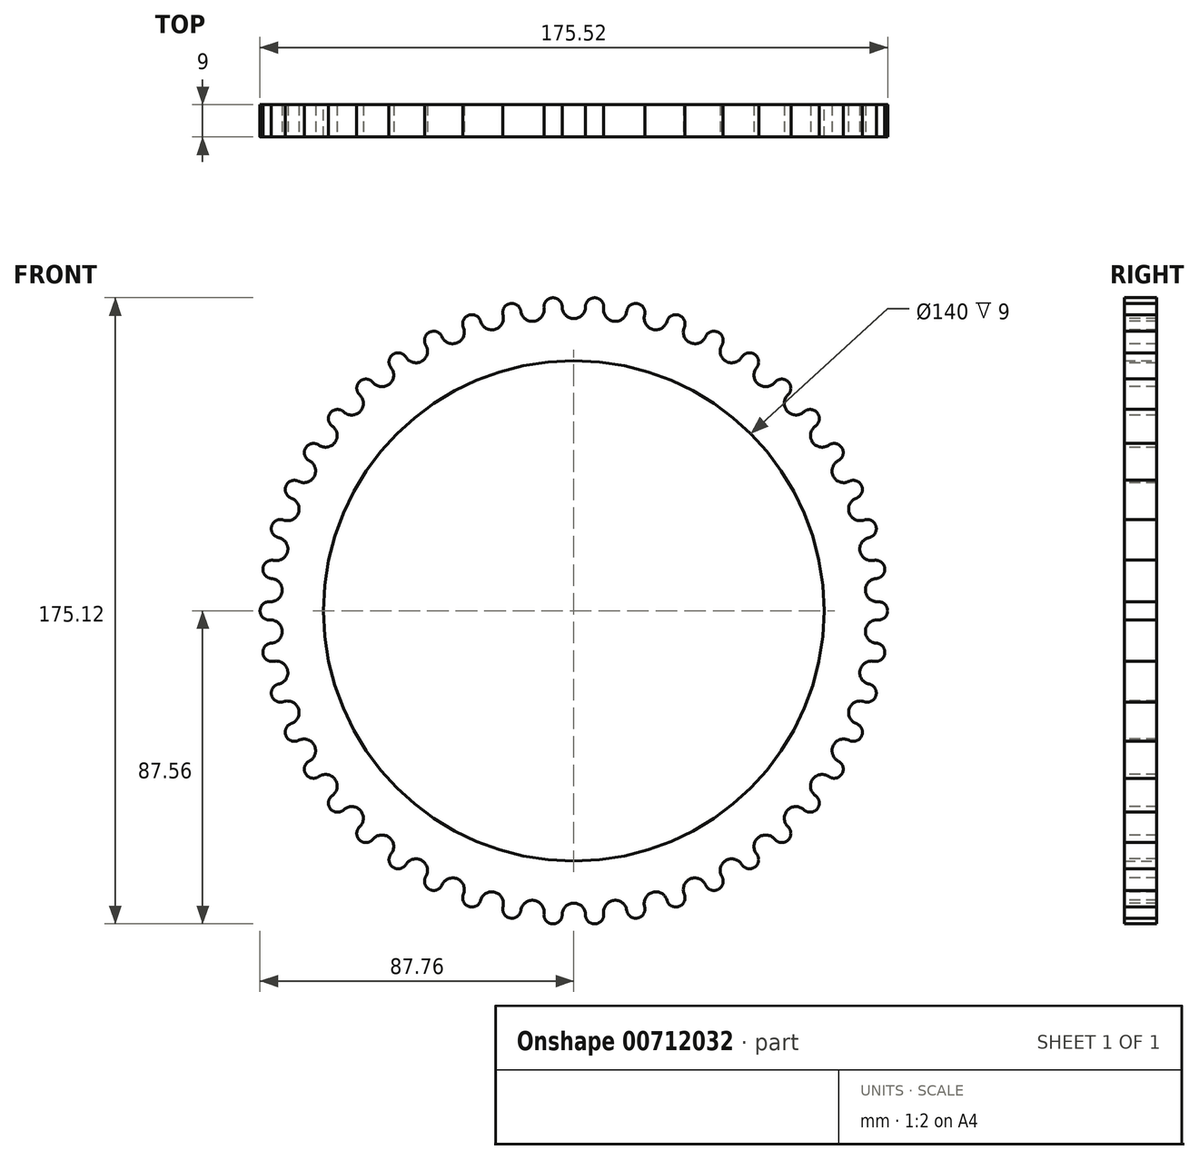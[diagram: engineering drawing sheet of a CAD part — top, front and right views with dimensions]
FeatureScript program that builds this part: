
annotation { "Feature Type Name" : "Feature", "Feature Type Description" : "" }
export const myFeature = defineFeature(function(context is Context, id is Id, definition is map)
    precondition{}
    {
        {
            var Q0;
            Q0=qCreatedBy(makeId("Front.planeOp"),FACE);
            var sketch = newSketch(context, id + "F0", { "sketchPlane" : qUnion([Q0])});
            skCircle(sketch, "E0", {"center": v(0, 0) * mm, "radius": 70 * mm});
            skCircle(sketch, "E1", {"center": v(0, 0) * mm, "radius": 80 * mm});
            skArc(sketch, "E2", {"start": v(4.8, -89.87) * mm, "mid": v(0, 90) * mm, "end": v(-4.8, -89.87) * mm});
            skArc(sketch, "E3", {"start": v(3, -85) * mm, "mid": v(0, -82) * mm, "end": v(-3, -85) * mm});
            skPoint(sketch, "E4.orphan", {"position": v(0, -90) * mm});
            skPoint(sketch, "E5.visualSharp", {"position": v(-3, -89.95) * mm});
            skPoint(sketch, "E6.visualSharp", {"position": v(3, -89.95) * mm});
            skLineSegment(sketch, "E7", {"start": v(0, -90) * mm, "end": v(0, -85) * mm});
            skLineSegment(sketch, "E8.1.0", {"start": v(3, 85) * mm, "end": v(3, 88.91) * mm});
            skArc(sketch, "E8.1.1", {"start": v(4.04, 89.9) * mm, "mid": v(3.3, 89.63) * mm, "end": v(3, 88.91) * mm});
            skArc(sketch, "E8.1.2", {"start": v(-3, 85) * mm, "mid": v(0, 82) * mm, "end": v(3, 85) * mm});
            skLineSegment(sketch, "E8.1.3", {"start": v(-3, 85) * mm, "end": v(-3, 88.91) * mm});
            skArc(sketch, "E8.1.4", {"start": v(-3, 88.91) * mm, "mid": v(-3.3, 89.63) * mm, "end": v(-4.04, 89.9) * mm});
            skLineSegment(sketch, "E9", {"start": v(-3, -86.96) * mm, "end": v(-3.8, -89.2) * mm});
            skLineSegment(sketch, "E10", {"start": v(3, -86.96) * mm, "end": v(3.8, -89.2) * mm});
            skPoint(sketch, "E11.visualSharp", {"position": v(-4.04, -89.9) * mm});
            skArc(sketch, "E11.filletArc", {"start": v(-4.8, -89.87) * mm, "mid": v(-4.18, -89.7) * mm, "end": v(-3.8, -89.2) * mm});
            skPoint(sketch, "E12.visualSharp", {"position": v(4.04, -89.9) * mm});
            skArc(sketch, "E12.filletArc", {"start": v(3.8, -89.2) * mm, "mid": v(4.18, -89.7) * mm, "end": v(4.8, -89.87) * mm});
            skArc(sketch, "E13.1.0", {"start": v(7.49, -89.69) * mm, "mid": v(8.07, -89.44) * mm, "end": v(8.39, -88.9) * mm});
            skLineSegment(sketch, "E13.1.1", {"start": v(8.87, -86.55) * mm, "end": v(8.39, -88.9) * mm});
            skLineSegment(sketch, "E13.1.2", {"start": v(8.6, -84.62) * mm, "end": v(9.13, -88.5) * mm});
            skArc(sketch, "E13.1.3", {"start": v(14.55, -83.8) * mm, "mid": v(11.17, -81.24) * mm, "end": v(8.6, -84.62) * mm});
            skLineSegment(sketch, "E13.1.4", {"start": v(14.55, -83.8) * mm, "end": v(15.08, -87.67) * mm});
            skLineSegment(sketch, "E13.1.5", {"start": v(14.81, -85.74) * mm, "end": v(15.9, -87.86) * mm});
            skArc(sketch, "E13.1.6", {"start": v(15.9, -87.86) * mm, "mid": v(16.36, -88.3) * mm, "end": v(16.99, -88.38) * mm});
            skArc(sketch, "E13.2.0", {"start": v(19.63, -87.83) * mm, "mid": v(20.17, -87.5) * mm, "end": v(20.41, -86.92) * mm});
            skLineSegment(sketch, "E13.2.1", {"start": v(20.57, -84.54) * mm, "end": v(20.41, -86.92) * mm});
            skLineSegment(sketch, "E13.2.2", {"start": v(20.04, -82.66) * mm, "end": v(21.1, -86.42) * mm});
            skArc(sketch, "E13.2.3", {"start": v(25.82, -81.04) * mm, "mid": v(22.12, -78.96) * mm, "end": v(20.04, -82.66) * mm});
            skLineSegment(sketch, "E13.2.4", {"start": v(25.82, -81.04) * mm, "end": v(26.88, -84.8) * mm});
            skLineSegment(sketch, "E13.2.5", {"start": v(26.35, -82.92) * mm, "end": v(27.72, -84.87) * mm});
            skArc(sketch, "E13.2.6", {"start": v(27.72, -84.87) * mm, "mid": v(28.23, -85.25) * mm, "end": v(28.86, -85.25) * mm});
            skArc(sketch, "E13.3.0", {"start": v(31.4, -84.34) * mm, "mid": v(31.9, -83.95) * mm, "end": v(32.06, -83.33) * mm});
            skLineSegment(sketch, "E13.3.1", {"start": v(31.9, -80.95) * mm, "end": v(32.06, -83.33) * mm});
            skLineSegment(sketch, "E13.3.2", {"start": v(31.11, -79.16) * mm, "end": v(32.67, -82.74) * mm});
            skArc(sketch, "E13.3.3", {"start": v(36.62, -76.77) * mm, "mid": v(32.67, -75.21) * mm, "end": v(31.11, -79.16) * mm});
            skLineSegment(sketch, "E13.3.4", {"start": v(36.62, -76.77) * mm, "end": v(38.17, -80.35) * mm});
            skLineSegment(sketch, "E13.3.5", {"start": v(37.4, -78.56) * mm, "end": v(39.02, -80.3) * mm});
            skArc(sketch, "E13.3.6", {"start": v(39.02, -80.3) * mm, "mid": v(39.58, -80.61) * mm, "end": v(40.2, -80.52) * mm});
            skArc(sketch, "E13.4.0", {"start": v(42.6, -79.28) * mm, "mid": v(43.03, -78.82) * mm, "end": v(43.1, -78.2) * mm});
            skLineSegment(sketch, "E13.4.1", {"start": v(42.62, -75.85) * mm, "end": v(43.1, -78.2) * mm});
            skLineSegment(sketch, "E13.4.2", {"start": v(41.6, -74.18) * mm, "end": v(43.63, -77.53) * mm});
            skArc(sketch, "E13.4.3", {"start": v(46.73, -71.07) * mm, "mid": v(42.6, -70.06) * mm, "end": v(41.6, -74.18) * mm});
            skLineSegment(sketch, "E13.4.4", {"start": v(46.73, -71.07) * mm, "end": v(48.76, -74.4) * mm});
            skLineSegment(sketch, "E13.4.5", {"start": v(47.74, -72.74) * mm, "end": v(49.6, -74.25) * mm});
            skArc(sketch, "E13.4.6", {"start": v(49.6, -74.25) * mm, "mid": v(50.18, -74.47) * mm, "end": v(50.8, -74.3) * mm});
            skArc(sketch, "E13.5.0", {"start": v(53, -72.74) * mm, "mid": v(53.37, -72.23) * mm, "end": v(53.35, -71.6) * mm});
            skLineSegment(sketch, "E13.5.1", {"start": v(52.55, -69.35) * mm, "end": v(53.35, -71.6) * mm});
            skLineSegment(sketch, "E13.5.2", {"start": v(51.32, -67.83) * mm, "end": v(53.78, -70.86) * mm});
            skArc(sketch, "E13.5.3", {"start": v(55.97, -64.04) * mm, "mid": v(51.75, -63.6) * mm, "end": v(51.32, -67.83) * mm});
            skLineSegment(sketch, "E13.5.4", {"start": v(55.97, -64.04) * mm, "end": v(58.44, -67.08) * mm});
            skLineSegment(sketch, "E13.5.5", {"start": v(57.2, -65.56) * mm, "end": v(59.24, -66.8) * mm});
            skArc(sketch, "E13.5.6", {"start": v(59.24, -66.8) * mm, "mid": v(59.86, -66.94) * mm, "end": v(60.44, -66.7) * mm});
            skArc(sketch, "E13.6.0", {"start": v(62.41, -64.85) * mm, "mid": v(62.7, -64.29) * mm, "end": v(62.6, -63.66) * mm});
            skLineSegment(sketch, "E13.6.1", {"start": v(61.5, -61.54) * mm, "end": v(62.6, -63.66) * mm});
            skLineSegment(sketch, "E13.6.2", {"start": v(60.07, -60.2) * mm, "end": v(62.93, -62.88) * mm});
            skArc(sketch, "E13.6.3", {"start": v(64.17, -55.82) * mm, "mid": v(59.93, -55.97) * mm, "end": v(60.07, -60.2) * mm});
            skLineSegment(sketch, "E13.6.4", {"start": v(64.17, -55.82) * mm, "end": v(67.03, -58.5) * mm});
            skLineSegment(sketch, "E13.6.5", {"start": v(65.6, -57.16) * mm, "end": v(67.79, -58.11) * mm});
            skArc(sketch, "E13.6.6", {"start": v(67.79, -58.11) * mm, "mid": v(68.42, -58.17) * mm, "end": v(68.95, -57.84) * mm});
            skArc(sketch, "E13.7.0", {"start": v(70.66, -55.74) * mm, "mid": v(70.87, -55.15) * mm, "end": v(70.7, -54.55) * mm});
            skLineSegment(sketch, "E13.7.1", {"start": v(69.3, -52.6) * mm, "end": v(70.7, -54.55) * mm});
            skLineSegment(sketch, "E13.7.2", {"start": v(67.71, -51.47) * mm, "end": v(70.9, -53.72) * mm});
            skArc(sketch, "E13.7.3", {"start": v(71.17, -46.57) * mm, "mid": v(67, -47.29) * mm, "end": v(67.71, -51.47) * mm});
            skLineSegment(sketch, "E13.7.4", {"start": v(71.17, -46.57) * mm, "end": v(74.37, -48.82) * mm});
            skLineSegment(sketch, "E13.7.5", {"start": v(72.77, -47.7) * mm, "end": v(75.07, -48.34) * mm});
            skArc(sketch, "E13.7.6", {"start": v(75.07, -48.34) * mm, "mid": v(75.7, -48.31) * mm, "end": v(76.19, -47.91) * mm});
            skArc(sketch, "E13.8.0", {"start": v(77.6, -45.6) * mm, "mid": v(77.72, -44.99) * mm, "end": v(77.46, -44.41) * mm});
            skLineSegment(sketch, "E13.8.1", {"start": v(75.83, -42.67) * mm, "end": v(77.46, -44.41) * mm});
            skLineSegment(sketch, "E13.8.2", {"start": v(74.1, -41.77) * mm, "end": v(77.56, -43.57) * mm});
            skArc(sketch, "E13.8.3", {"start": v(76.85, -36.44) * mm, "mid": v(72.8, -37.73) * mm, "end": v(74.1, -41.77) * mm});
            skLineSegment(sketch, "E13.8.4", {"start": v(76.85, -36.44) * mm, "end": v(80.32, -38.24) * mm});
            skLineSegment(sketch, "E13.8.5", {"start": v(78.59, -37.34) * mm, "end": v(80.95, -37.67) * mm});
            skArc(sketch, "E13.8.6", {"start": v(80.95, -37.67) * mm, "mid": v(81.57, -37.56) * mm, "end": v(82, -37.1) * mm});
            skArc(sketch, "E13.9.0", {"start": v(83.08, -34.61) * mm, "mid": v(83.12, -33.98) * mm, "end": v(82.79, -33.45) * mm});
            skLineSegment(sketch, "E13.9.1", {"start": v(80.93, -31.95) * mm, "end": v(82.79, -33.45) * mm});
            skLineSegment(sketch, "E13.9.2", {"start": v(79.09, -31.3) * mm, "end": v(82.77, -32.6) * mm});
            skArc(sketch, "E13.9.3", {"start": v(81.1, -25.64) * mm, "mid": v(77.27, -27.46) * mm, "end": v(79.09, -31.3) * mm});
            skLineSegment(sketch, "E13.9.4", {"start": v(81.1, -25.64) * mm, "end": v(84.78, -26.95) * mm});
            skLineSegment(sketch, "E13.9.5", {"start": v(82.94, -26.3) * mm, "end": v(85.33, -26.3) * mm});
            skArc(sketch, "E13.9.6", {"start": v(85.33, -26.3) * mm, "mid": v(85.93, -26.1) * mm, "end": v(86.29, -25.58) * mm});
            skArc(sketch, "E13.10.0", {"start": v(87.02, -22.98) * mm, "mid": v(86.98, -22.35) * mm, "end": v(86.57, -21.87) * mm});
            skLineSegment(sketch, "E13.10.1", {"start": v(84.53, -20.63) * mm, "end": v(86.57, -21.87) * mm});
            skLineSegment(sketch, "E13.10.2", {"start": v(82.61, -20.23) * mm, "end": v(86.44, -21.03) * mm});
            skArc(sketch, "E13.10.3", {"start": v(83.83, -14.36) * mm, "mid": v(80.28, -16.68) * mm, "end": v(82.61, -20.23) * mm});
            skLineSegment(sketch, "E13.10.4", {"start": v(83.83, -14.36) * mm, "end": v(87.66, -15.15) * mm});
            skLineSegment(sketch, "E13.10.5", {"start": v(85.75, -14.75) * mm, "end": v(88.11, -14.43) * mm});
            skArc(sketch, "E13.10.6", {"start": v(88.11, -14.43) * mm, "mid": v(88.68, -14.15) * mm, "end": v(88.97, -13.6) * mm});
            skArc(sketch, "E13.11.0", {"start": v(89.34, -10.91) * mm, "mid": v(89.21, -10.3) * mm, "end": v(88.74, -9.88) * mm});
            skLineSegment(sketch, "E13.11.1", {"start": v(86.55, -8.93) * mm, "end": v(88.74, -9.88) * mm});
            skLineSegment(sketch, "E13.11.2", {"start": v(84.6, -8.8) * mm, "end": v(88.5, -9.06) * mm});
            skArc(sketch, "E13.11.3", {"start": v(85, -2.8) * mm, "mid": v(81.8, -5.6) * mm, "end": v(84.6, -8.8) * mm});
            skLineSegment(sketch, "E13.11.4", {"start": v(85, -2.8) * mm, "end": v(88.9, -3.07) * mm});
            skLineSegment(sketch, "E13.11.5", {"start": v(86.96, -2.94) * mm, "end": v(89.26, -2.3) * mm});
            skArc(sketch, "E13.11.6", {"start": v(89.26, -2.3) * mm, "mid": v(89.78, -1.95) * mm, "end": v(89.99, -1.35) * mm});
            skArc(sketch, "E13.12.0", {"start": v(89.99, 1.35) * mm, "mid": v(89.78, 1.95) * mm, "end": v(89.26, 2.3) * mm});
            skLineSegment(sketch, "E13.12.1", {"start": v(86.96, 2.94) * mm, "end": v(89.26, 2.3) * mm});
            skLineSegment(sketch, "E13.12.2", {"start": v(85, 2.8) * mm, "end": v(88.9, 3.07) * mm});
            skArc(sketch, "E13.12.3", {"start": v(84.6, 8.8) * mm, "mid": v(81.8, 5.6) * mm, "end": v(85, 2.8) * mm});
            skLineSegment(sketch, "E13.12.4", {"start": v(84.6, 8.8) * mm, "end": v(88.5, 9.06) * mm});
            skLineSegment(sketch, "E13.12.5", {"start": v(86.55, 8.93) * mm, "end": v(88.74, 9.88) * mm});
            skArc(sketch, "E13.12.6", {"start": v(88.74, 9.88) * mm, "mid": v(89.21, 10.3) * mm, "end": v(89.34, 10.91) * mm});
            skArc(sketch, "E13.13.0", {"start": v(88.97, 13.6) * mm, "mid": v(88.68, 14.15) * mm, "end": v(88.11, 14.43) * mm});
            skLineSegment(sketch, "E13.13.1", {"start": v(85.75, 14.75) * mm, "end": v(88.11, 14.43) * mm});
            skLineSegment(sketch, "E13.13.2", {"start": v(83.83, 14.36) * mm, "end": v(87.66, 15.15) * mm});
            skArc(sketch, "E13.13.3", {"start": v(82.61, 20.23) * mm, "mid": v(80.28, 16.68) * mm, "end": v(83.83, 14.36) * mm});
            skLineSegment(sketch, "E13.13.4", {"start": v(82.61, 20.23) * mm, "end": v(86.44, 21.03) * mm});
            skLineSegment(sketch, "E13.13.5", {"start": v(84.53, 20.63) * mm, "end": v(86.57, 21.87) * mm});
            skArc(sketch, "E13.13.6", {"start": v(86.57, 21.87) * mm, "mid": v(86.98, 22.35) * mm, "end": v(87.02, 22.98) * mm});
            skArc(sketch, "E13.14.0", {"start": v(86.29, 25.58) * mm, "mid": v(85.93, 26.1) * mm, "end": v(85.33, 26.3) * mm});
            skLineSegment(sketch, "E13.14.1", {"start": v(82.94, 26.3) * mm, "end": v(85.33, 26.3) * mm});
            skLineSegment(sketch, "E13.14.2", {"start": v(81.1, 25.64) * mm, "end": v(84.78, 26.95) * mm});
            skArc(sketch, "E13.14.3", {"start": v(79.09, 31.3) * mm, "mid": v(77.27, 27.46) * mm, "end": v(81.1, 25.64) * mm});
            skLineSegment(sketch, "E13.14.4", {"start": v(79.09, 31.3) * mm, "end": v(82.77, 32.6) * mm});
            skLineSegment(sketch, "E13.14.5", {"start": v(80.93, 31.95) * mm, "end": v(82.79, 33.45) * mm});
            skArc(sketch, "E13.14.6", {"start": v(82.79, 33.45) * mm, "mid": v(83.12, 33.98) * mm, "end": v(83.08, 34.61) * mm});
            skArc(sketch, "E13.15.0", {"start": v(82, 37.1) * mm, "mid": v(81.57, 37.56) * mm, "end": v(80.95, 37.67) * mm});
            skLineSegment(sketch, "E13.15.1", {"start": v(78.59, 37.34) * mm, "end": v(80.95, 37.67) * mm});
            skLineSegment(sketch, "E13.15.2", {"start": v(76.85, 36.44) * mm, "end": v(80.32, 38.24) * mm});
            skArc(sketch, "E13.15.3", {"start": v(74.1, 41.77) * mm, "mid": v(72.8, 37.73) * mm, "end": v(76.85, 36.44) * mm});
            skLineSegment(sketch, "E13.15.4", {"start": v(74.1, 41.77) * mm, "end": v(77.56, 43.57) * mm});
            skLineSegment(sketch, "E13.15.5", {"start": v(75.83, 42.67) * mm, "end": v(77.46, 44.41) * mm});
            skArc(sketch, "E13.15.6", {"start": v(77.46, 44.41) * mm, "mid": v(77.72, 44.99) * mm, "end": v(77.6, 45.6) * mm});
            skArc(sketch, "E13.16.0", {"start": v(76.19, 47.91) * mm, "mid": v(75.7, 48.31) * mm, "end": v(75.07, 48.34) * mm});
            skLineSegment(sketch, "E13.16.1", {"start": v(72.77, 47.7) * mm, "end": v(75.07, 48.34) * mm});
            skLineSegment(sketch, "E13.16.2", {"start": v(71.17, 46.57) * mm, "end": v(74.37, 48.82) * mm});
            skArc(sketch, "E13.16.3", {"start": v(67.71, 51.47) * mm, "mid": v(67, 47.29) * mm, "end": v(71.17, 46.57) * mm});
            skLineSegment(sketch, "E13.16.4", {"start": v(67.71, 51.47) * mm, "end": v(70.9, 53.72) * mm});
            skLineSegment(sketch, "E13.16.5", {"start": v(69.3, 52.6) * mm, "end": v(70.7, 54.55) * mm});
            skArc(sketch, "E13.16.6", {"start": v(70.7, 54.55) * mm, "mid": v(70.87, 55.15) * mm, "end": v(70.66, 55.74) * mm});
            skArc(sketch, "E13.17.0", {"start": v(68.95, 57.84) * mm, "mid": v(68.42, 58.17) * mm, "end": v(67.79, 58.11) * mm});
            skLineSegment(sketch, "E13.17.1", {"start": v(65.6, 57.16) * mm, "end": v(67.79, 58.11) * mm});
            skLineSegment(sketch, "E13.17.2", {"start": v(64.17, 55.82) * mm, "end": v(67.03, 58.5) * mm});
            skArc(sketch, "E13.17.3", {"start": v(60.07, 60.2) * mm, "mid": v(59.93, 55.97) * mm, "end": v(64.17, 55.82) * mm});
            skLineSegment(sketch, "E13.17.4", {"start": v(60.07, 60.2) * mm, "end": v(62.93, 62.88) * mm});
            skLineSegment(sketch, "E13.17.5", {"start": v(61.5, 61.54) * mm, "end": v(62.6, 63.66) * mm});
            skArc(sketch, "E13.17.6", {"start": v(62.6, 63.66) * mm, "mid": v(62.7, 64.29) * mm, "end": v(62.41, 64.85) * mm});
            skArc(sketch, "E13.18.0", {"start": v(60.44, 66.7) * mm, "mid": v(59.86, 66.94) * mm, "end": v(59.24, 66.8) * mm});
            skLineSegment(sketch, "E13.18.1", {"start": v(57.2, 65.56) * mm, "end": v(59.24, 66.8) * mm});
            skLineSegment(sketch, "E13.18.2", {"start": v(55.97, 64.04) * mm, "end": v(58.44, 67.08) * mm});
            skArc(sketch, "E13.18.3", {"start": v(51.32, 67.83) * mm, "mid": v(51.75, 63.6) * mm, "end": v(55.97, 64.04) * mm});
            skLineSegment(sketch, "E13.18.4", {"start": v(51.32, 67.83) * mm, "end": v(53.78, 70.86) * mm});
            skLineSegment(sketch, "E13.18.5", {"start": v(52.55, 69.35) * mm, "end": v(53.35, 71.6) * mm});
            skArc(sketch, "E13.18.6", {"start": v(53.35, 71.6) * mm, "mid": v(53.37, 72.23) * mm, "end": v(53, 72.74) * mm});
            skArc(sketch, "E13.19.0", {"start": v(50.8, 74.3) * mm, "mid": v(50.18, 74.47) * mm, "end": v(49.6, 74.25) * mm});
            skLineSegment(sketch, "E13.19.1", {"start": v(47.74, 72.74) * mm, "end": v(49.6, 74.25) * mm});
            skLineSegment(sketch, "E13.19.2", {"start": v(46.73, 71.07) * mm, "end": v(48.76, 74.4) * mm});
            skArc(sketch, "E13.19.3", {"start": v(41.6, 74.18) * mm, "mid": v(42.6, 70.06) * mm, "end": v(46.73, 71.07) * mm});
            skLineSegment(sketch, "E13.19.4", {"start": v(41.6, 74.18) * mm, "end": v(43.63, 77.53) * mm});
            skLineSegment(sketch, "E13.19.5", {"start": v(42.62, 75.85) * mm, "end": v(43.1, 78.2) * mm});
            skArc(sketch, "E13.19.6", {"start": v(43.1, 78.2) * mm, "mid": v(43.03, 78.82) * mm, "end": v(42.6, 79.28) * mm});
            skArc(sketch, "E13.20.0", {"start": v(40.2, 80.52) * mm, "mid": v(39.58, 80.61) * mm, "end": v(39.02, 80.3) * mm});
            skLineSegment(sketch, "E13.20.1", {"start": v(37.4, 78.56) * mm, "end": v(39.02, 80.3) * mm});
            skLineSegment(sketch, "E13.20.2", {"start": v(36.62, 76.77) * mm, "end": v(38.17, 80.35) * mm});
            skArc(sketch, "E13.20.3", {"start": v(31.11, 79.16) * mm, "mid": v(32.67, 75.21) * mm, "end": v(36.62, 76.77) * mm});
            skLineSegment(sketch, "E13.20.4", {"start": v(31.11, 79.16) * mm, "end": v(32.67, 82.74) * mm});
            skLineSegment(sketch, "E13.20.5", {"start": v(31.9, 80.95) * mm, "end": v(32.06, 83.33) * mm});
            skArc(sketch, "E13.20.6", {"start": v(32.06, 83.33) * mm, "mid": v(31.9, 83.95) * mm, "end": v(31.4, 84.34) * mm});
            skArc(sketch, "E13.21.0", {"start": v(28.86, 85.25) * mm, "mid": v(28.23, 85.25) * mm, "end": v(27.72, 84.87) * mm});
            skLineSegment(sketch, "E13.21.1", {"start": v(26.35, 82.92) * mm, "end": v(27.72, 84.87) * mm});
            skLineSegment(sketch, "E13.21.2", {"start": v(25.82, 81.04) * mm, "end": v(26.88, 84.8) * mm});
            skArc(sketch, "E13.21.3", {"start": v(20.04, 82.66) * mm, "mid": v(22.12, 78.96) * mm, "end": v(25.82, 81.04) * mm});
            skLineSegment(sketch, "E13.21.4", {"start": v(20.04, 82.66) * mm, "end": v(21.1, 86.42) * mm});
            skLineSegment(sketch, "E13.21.5", {"start": v(20.57, 84.54) * mm, "end": v(20.41, 86.92) * mm});
            skArc(sketch, "E13.21.6", {"start": v(20.41, 86.92) * mm, "mid": v(20.17, 87.5) * mm, "end": v(19.63, 87.83) * mm});
            skArc(sketch, "E13.22.0", {"start": v(16.99, 88.38) * mm, "mid": v(16.36, 88.3) * mm, "end": v(15.9, 87.86) * mm});
            skLineSegment(sketch, "E13.22.1", {"start": v(14.81, 85.74) * mm, "end": v(15.9, 87.86) * mm});
            skLineSegment(sketch, "E13.22.2", {"start": v(14.55, 83.8) * mm, "end": v(15.08, 87.67) * mm});
            skArc(sketch, "E13.22.3", {"start": v(8.6, 84.62) * mm, "mid": v(11.17, 81.24) * mm, "end": v(14.55, 83.8) * mm});
            skLineSegment(sketch, "E13.22.4", {"start": v(8.6, 84.62) * mm, "end": v(9.13, 88.5) * mm});
            skLineSegment(sketch, "E13.22.5", {"start": v(8.87, 86.55) * mm, "end": v(8.39, 88.9) * mm});
            skArc(sketch, "E13.22.6", {"start": v(8.39, 88.9) * mm, "mid": v(8.07, 89.44) * mm, "end": v(7.49, 89.69) * mm});
            skArc(sketch, "E13.23.0", {"start": v(4.8, 89.87) * mm, "mid": v(4.18, 89.7) * mm, "end": v(3.8, 89.2) * mm});
            skLineSegment(sketch, "E13.23.1", {"start": v(3, 86.96) * mm, "end": v(3.8, 89.2) * mm});
            skLineSegment(sketch, "E13.23.5", {"start": v(-3, 86.96) * mm, "end": v(-3.8, 89.2) * mm});
            skArc(sketch, "E13.23.6", {"start": v(-3.8, 89.2) * mm, "mid": v(-4.18, 89.7) * mm, "end": v(-4.8, 89.87) * mm});
            skArc(sketch, "E13.24.0", {"start": v(-7.49, 89.69) * mm, "mid": v(-8.07, 89.44) * mm, "end": v(-8.39, 88.9) * mm});
            skLineSegment(sketch, "E13.24.1", {"start": v(-8.87, 86.55) * mm, "end": v(-8.39, 88.9) * mm});
            skLineSegment(sketch, "E13.24.2", {"start": v(-8.6, 84.62) * mm, "end": v(-9.13, 88.5) * mm});
            skArc(sketch, "E13.24.3", {"start": v(-14.55, 83.8) * mm, "mid": v(-11.17, 81.24) * mm, "end": v(-8.6, 84.62) * mm});
            skLineSegment(sketch, "E13.24.4", {"start": v(-14.55, 83.8) * mm, "end": v(-15.08, 87.67) * mm});
            skLineSegment(sketch, "E13.24.5", {"start": v(-14.81, 85.74) * mm, "end": v(-15.9, 87.86) * mm});
            skArc(sketch, "E13.24.6", {"start": v(-15.9, 87.86) * mm, "mid": v(-16.36, 88.3) * mm, "end": v(-16.99, 88.38) * mm});
            skArc(sketch, "E13.25.0", {"start": v(-19.63, 87.83) * mm, "mid": v(-20.17, 87.5) * mm, "end": v(-20.41, 86.92) * mm});
            skLineSegment(sketch, "E13.25.1", {"start": v(-20.57, 84.54) * mm, "end": v(-20.41, 86.92) * mm});
            skLineSegment(sketch, "E13.25.2", {"start": v(-20.04, 82.66) * mm, "end": v(-21.1, 86.42) * mm});
            skArc(sketch, "E13.25.3", {"start": v(-25.82, 81.04) * mm, "mid": v(-22.12, 78.96) * mm, "end": v(-20.04, 82.66) * mm});
            skLineSegment(sketch, "E13.25.4", {"start": v(-25.82, 81.04) * mm, "end": v(-26.88, 84.8) * mm});
            skLineSegment(sketch, "E13.25.5", {"start": v(-26.35, 82.92) * mm, "end": v(-27.72, 84.87) * mm});
            skArc(sketch, "E13.25.6", {"start": v(-27.72, 84.87) * mm, "mid": v(-28.23, 85.25) * mm, "end": v(-28.86, 85.25) * mm});
            skArc(sketch, "E13.26.0", {"start": v(-31.4, 84.34) * mm, "mid": v(-31.9, 83.95) * mm, "end": v(-32.06, 83.33) * mm});
            skLineSegment(sketch, "E13.26.1", {"start": v(-31.9, 80.95) * mm, "end": v(-32.06, 83.33) * mm});
            skLineSegment(sketch, "E13.26.2", {"start": v(-31.11, 79.16) * mm, "end": v(-32.67, 82.74) * mm});
            skArc(sketch, "E13.26.3", {"start": v(-36.62, 76.77) * mm, "mid": v(-32.67, 75.21) * mm, "end": v(-31.11, 79.16) * mm});
            skLineSegment(sketch, "E13.26.4", {"start": v(-36.62, 76.77) * mm, "end": v(-38.17, 80.35) * mm});
            skLineSegment(sketch, "E13.26.5", {"start": v(-37.4, 78.56) * mm, "end": v(-39.02, 80.3) * mm});
            skArc(sketch, "E13.26.6", {"start": v(-39.02, 80.3) * mm, "mid": v(-39.58, 80.61) * mm, "end": v(-40.2, 80.52) * mm});
            skArc(sketch, "E13.27.0", {"start": v(-42.6, 79.28) * mm, "mid": v(-43.03, 78.82) * mm, "end": v(-43.1, 78.2) * mm});
            skLineSegment(sketch, "E13.27.1", {"start": v(-42.62, 75.85) * mm, "end": v(-43.1, 78.2) * mm});
            skLineSegment(sketch, "E13.27.2", {"start": v(-41.6, 74.18) * mm, "end": v(-43.63, 77.53) * mm});
            skArc(sketch, "E13.27.3", {"start": v(-46.73, 71.07) * mm, "mid": v(-42.6, 70.06) * mm, "end": v(-41.6, 74.18) * mm});
            skLineSegment(sketch, "E13.27.4", {"start": v(-46.73, 71.07) * mm, "end": v(-48.76, 74.4) * mm});
            skLineSegment(sketch, "E13.27.5", {"start": v(-47.74, 72.74) * mm, "end": v(-49.6, 74.25) * mm});
            skArc(sketch, "E13.27.6", {"start": v(-49.6, 74.25) * mm, "mid": v(-50.18, 74.47) * mm, "end": v(-50.8, 74.3) * mm});
            skArc(sketch, "E13.28.0", {"start": v(-53, 72.74) * mm, "mid": v(-53.37, 72.23) * mm, "end": v(-53.35, 71.6) * mm});
            skLineSegment(sketch, "E13.28.1", {"start": v(-52.55, 69.35) * mm, "end": v(-53.35, 71.6) * mm});
            skLineSegment(sketch, "E13.28.2", {"start": v(-51.32, 67.83) * mm, "end": v(-53.78, 70.86) * mm});
            skArc(sketch, "E13.28.3", {"start": v(-55.97, 64.04) * mm, "mid": v(-51.75, 63.6) * mm, "end": v(-51.32, 67.83) * mm});
            skLineSegment(sketch, "E13.28.4", {"start": v(-55.97, 64.04) * mm, "end": v(-58.44, 67.08) * mm});
            skLineSegment(sketch, "E13.28.5", {"start": v(-57.2, 65.56) * mm, "end": v(-59.24, 66.8) * mm});
            skArc(sketch, "E13.28.6", {"start": v(-59.24, 66.8) * mm, "mid": v(-59.86, 66.94) * mm, "end": v(-60.44, 66.7) * mm});
            skArc(sketch, "E13.29.0", {"start": v(-62.41, 64.85) * mm, "mid": v(-62.7, 64.29) * mm, "end": v(-62.6, 63.66) * mm});
            skLineSegment(sketch, "E13.29.1", {"start": v(-61.5, 61.54) * mm, "end": v(-62.6, 63.66) * mm});
            skLineSegment(sketch, "E13.29.2", {"start": v(-60.07, 60.2) * mm, "end": v(-62.93, 62.88) * mm});
            skArc(sketch, "E13.29.3", {"start": v(-64.17, 55.82) * mm, "mid": v(-59.93, 55.97) * mm, "end": v(-60.07, 60.2) * mm});
            skLineSegment(sketch, "E13.29.4", {"start": v(-64.17, 55.82) * mm, "end": v(-67.03, 58.5) * mm});
            skLineSegment(sketch, "E13.29.5", {"start": v(-65.6, 57.16) * mm, "end": v(-67.79, 58.11) * mm});
            skArc(sketch, "E13.29.6", {"start": v(-67.79, 58.11) * mm, "mid": v(-68.42, 58.17) * mm, "end": v(-68.95, 57.84) * mm});
            skArc(sketch, "E13.30.0", {"start": v(-70.66, 55.74) * mm, "mid": v(-70.87, 55.15) * mm, "end": v(-70.7, 54.55) * mm});
            skLineSegment(sketch, "E13.30.1", {"start": v(-69.3, 52.6) * mm, "end": v(-70.7, 54.55) * mm});
            skLineSegment(sketch, "E13.30.2", {"start": v(-67.71, 51.47) * mm, "end": v(-70.9, 53.72) * mm});
            skArc(sketch, "E13.30.3", {"start": v(-71.17, 46.57) * mm, "mid": v(-67, 47.29) * mm, "end": v(-67.71, 51.47) * mm});
            skLineSegment(sketch, "E13.30.4", {"start": v(-71.17, 46.57) * mm, "end": v(-74.37, 48.82) * mm});
            skLineSegment(sketch, "E13.30.5", {"start": v(-72.77, 47.7) * mm, "end": v(-75.07, 48.34) * mm});
            skArc(sketch, "E13.30.6", {"start": v(-75.07, 48.34) * mm, "mid": v(-75.7, 48.31) * mm, "end": v(-76.19, 47.91) * mm});
            skArc(sketch, "E13.31.0", {"start": v(-77.6, 45.6) * mm, "mid": v(-77.72, 44.99) * mm, "end": v(-77.46, 44.41) * mm});
            skLineSegment(sketch, "E13.31.1", {"start": v(-75.83, 42.67) * mm, "end": v(-77.46, 44.41) * mm});
            skLineSegment(sketch, "E13.31.2", {"start": v(-74.1, 41.77) * mm, "end": v(-77.56, 43.57) * mm});
            skArc(sketch, "E13.31.3", {"start": v(-76.85, 36.44) * mm, "mid": v(-72.8, 37.73) * mm, "end": v(-74.1, 41.77) * mm});
            skLineSegment(sketch, "E13.31.4", {"start": v(-76.85, 36.44) * mm, "end": v(-80.32, 38.24) * mm});
            skLineSegment(sketch, "E13.31.5", {"start": v(-78.59, 37.34) * mm, "end": v(-80.95, 37.67) * mm});
            skArc(sketch, "E13.31.6", {"start": v(-80.95, 37.67) * mm, "mid": v(-81.57, 37.56) * mm, "end": v(-82, 37.1) * mm});
            skArc(sketch, "E13.32.0", {"start": v(-83.08, 34.61) * mm, "mid": v(-83.12, 33.98) * mm, "end": v(-82.79, 33.45) * mm});
            skLineSegment(sketch, "E13.32.1", {"start": v(-80.93, 31.95) * mm, "end": v(-82.79, 33.45) * mm});
            skLineSegment(sketch, "E13.32.2", {"start": v(-79.09, 31.3) * mm, "end": v(-82.77, 32.6) * mm});
            skArc(sketch, "E13.32.3", {"start": v(-81.1, 25.64) * mm, "mid": v(-77.27, 27.46) * mm, "end": v(-79.09, 31.3) * mm});
            skLineSegment(sketch, "E13.32.4", {"start": v(-81.1, 25.64) * mm, "end": v(-84.78, 26.95) * mm});
            skLineSegment(sketch, "E13.32.5", {"start": v(-82.94, 26.3) * mm, "end": v(-85.33, 26.3) * mm});
            skArc(sketch, "E13.32.6", {"start": v(-85.33, 26.3) * mm, "mid": v(-85.93, 26.1) * mm, "end": v(-86.29, 25.58) * mm});
            skArc(sketch, "E13.33.0", {"start": v(-87.02, 22.98) * mm, "mid": v(-86.98, 22.35) * mm, "end": v(-86.57, 21.87) * mm});
            skLineSegment(sketch, "E13.33.1", {"start": v(-84.53, 20.63) * mm, "end": v(-86.57, 21.87) * mm});
            skLineSegment(sketch, "E13.33.2", {"start": v(-82.61, 20.23) * mm, "end": v(-86.44, 21.03) * mm});
            skArc(sketch, "E13.33.3", {"start": v(-83.83, 14.36) * mm, "mid": v(-80.28, 16.68) * mm, "end": v(-82.61, 20.23) * mm});
            skLineSegment(sketch, "E13.33.4", {"start": v(-83.83, 14.36) * mm, "end": v(-87.66, 15.15) * mm});
            skLineSegment(sketch, "E13.33.5", {"start": v(-85.75, 14.75) * mm, "end": v(-88.11, 14.43) * mm});
            skArc(sketch, "E13.33.6", {"start": v(-88.11, 14.43) * mm, "mid": v(-88.68, 14.15) * mm, "end": v(-88.97, 13.6) * mm});
            skArc(sketch, "E13.34.0", {"start": v(-89.34, 10.91) * mm, "mid": v(-89.21, 10.3) * mm, "end": v(-88.74, 9.88) * mm});
            skLineSegment(sketch, "E13.34.1", {"start": v(-86.55, 8.93) * mm, "end": v(-88.74, 9.88) * mm});
            skLineSegment(sketch, "E13.34.2", {"start": v(-84.6, 8.8) * mm, "end": v(-88.5, 9.06) * mm});
            skArc(sketch, "E13.34.3", {"start": v(-85, 2.8) * mm, "mid": v(-81.8, 5.6) * mm, "end": v(-84.6, 8.8) * mm});
            skLineSegment(sketch, "E13.34.4", {"start": v(-85, 2.8) * mm, "end": v(-88.9, 3.07) * mm});
            skLineSegment(sketch, "E13.34.5", {"start": v(-86.96, 2.94) * mm, "end": v(-89.26, 2.3) * mm});
            skArc(sketch, "E13.34.6", {"start": v(-89.26, 2.3) * mm, "mid": v(-89.78, 1.95) * mm, "end": v(-89.99, 1.35) * mm});
            skArc(sketch, "E13.35.0", {"start": v(-89.99, -1.35) * mm, "mid": v(-89.78, -1.95) * mm, "end": v(-89.26, -2.3) * mm});
            skLineSegment(sketch, "E13.35.1", {"start": v(-86.96, -2.94) * mm, "end": v(-89.26, -2.3) * mm});
            skLineSegment(sketch, "E13.35.2", {"start": v(-85, -2.8) * mm, "end": v(-88.9, -3.07) * mm});
            skArc(sketch, "E13.35.3", {"start": v(-84.6, -8.8) * mm, "mid": v(-81.8, -5.6) * mm, "end": v(-85, -2.8) * mm});
            skLineSegment(sketch, "E13.35.4", {"start": v(-84.6, -8.8) * mm, "end": v(-88.5, -9.06) * mm});
            skLineSegment(sketch, "E13.35.5", {"start": v(-86.55, -8.93) * mm, "end": v(-88.74, -9.88) * mm});
            skArc(sketch, "E13.35.6", {"start": v(-88.74, -9.88) * mm, "mid": v(-89.21, -10.3) * mm, "end": v(-89.34, -10.91) * mm});
            skArc(sketch, "E13.36.0", {"start": v(-88.97, -13.6) * mm, "mid": v(-88.68, -14.15) * mm, "end": v(-88.11, -14.43) * mm});
            skLineSegment(sketch, "E13.36.1", {"start": v(-85.75, -14.75) * mm, "end": v(-88.11, -14.43) * mm});
            skLineSegment(sketch, "E13.36.2", {"start": v(-83.83, -14.36) * mm, "end": v(-87.66, -15.15) * mm});
            skArc(sketch, "E13.36.3", {"start": v(-82.61, -20.23) * mm, "mid": v(-80.28, -16.68) * mm, "end": v(-83.83, -14.36) * mm});
            skLineSegment(sketch, "E13.36.4", {"start": v(-82.61, -20.23) * mm, "end": v(-86.44, -21.03) * mm});
            skLineSegment(sketch, "E13.36.5", {"start": v(-84.53, -20.63) * mm, "end": v(-86.57, -21.87) * mm});
            skArc(sketch, "E13.36.6", {"start": v(-86.57, -21.87) * mm, "mid": v(-86.98, -22.35) * mm, "end": v(-87.02, -22.98) * mm});
            skArc(sketch, "E13.37.0", {"start": v(-86.29, -25.58) * mm, "mid": v(-85.93, -26.1) * mm, "end": v(-85.33, -26.3) * mm});
            skLineSegment(sketch, "E13.37.1", {"start": v(-82.94, -26.3) * mm, "end": v(-85.33, -26.3) * mm});
            skLineSegment(sketch, "E13.37.2", {"start": v(-81.1, -25.64) * mm, "end": v(-84.78, -26.95) * mm});
            skArc(sketch, "E13.37.3", {"start": v(-79.09, -31.3) * mm, "mid": v(-77.27, -27.46) * mm, "end": v(-81.1, -25.64) * mm});
            skLineSegment(sketch, "E13.37.4", {"start": v(-79.09, -31.3) * mm, "end": v(-82.77, -32.6) * mm});
            skLineSegment(sketch, "E13.37.5", {"start": v(-80.93, -31.95) * mm, "end": v(-82.79, -33.45) * mm});
            skArc(sketch, "E13.37.6", {"start": v(-82.79, -33.45) * mm, "mid": v(-83.12, -33.98) * mm, "end": v(-83.08, -34.61) * mm});
            skArc(sketch, "E13.38.0", {"start": v(-82, -37.1) * mm, "mid": v(-81.57, -37.56) * mm, "end": v(-80.95, -37.67) * mm});
            skLineSegment(sketch, "E13.38.1", {"start": v(-78.59, -37.34) * mm, "end": v(-80.95, -37.67) * mm});
            skLineSegment(sketch, "E13.38.2", {"start": v(-76.85, -36.44) * mm, "end": v(-80.32, -38.24) * mm});
            skArc(sketch, "E13.38.3", {"start": v(-74.1, -41.77) * mm, "mid": v(-72.8, -37.73) * mm, "end": v(-76.85, -36.44) * mm});
            skLineSegment(sketch, "E13.38.4", {"start": v(-74.1, -41.77) * mm, "end": v(-77.56, -43.57) * mm});
            skLineSegment(sketch, "E13.38.5", {"start": v(-75.83, -42.67) * mm, "end": v(-77.46, -44.41) * mm});
            skArc(sketch, "E13.38.6", {"start": v(-77.46, -44.41) * mm, "mid": v(-77.72, -44.99) * mm, "end": v(-77.6, -45.6) * mm});
            skArc(sketch, "E13.39.0", {"start": v(-76.19, -47.91) * mm, "mid": v(-75.7, -48.31) * mm, "end": v(-75.07, -48.34) * mm});
            skLineSegment(sketch, "E13.39.1", {"start": v(-72.77, -47.7) * mm, "end": v(-75.07, -48.34) * mm});
            skLineSegment(sketch, "E13.39.2", {"start": v(-71.17, -46.57) * mm, "end": v(-74.37, -48.82) * mm});
            skArc(sketch, "E13.39.3", {"start": v(-67.71, -51.47) * mm, "mid": v(-67, -47.29) * mm, "end": v(-71.17, -46.57) * mm});
            skLineSegment(sketch, "E13.39.4", {"start": v(-67.71, -51.47) * mm, "end": v(-70.9, -53.72) * mm});
            skLineSegment(sketch, "E13.39.5", {"start": v(-69.3, -52.6) * mm, "end": v(-70.7, -54.55) * mm});
            skArc(sketch, "E13.39.6", {"start": v(-70.7, -54.55) * mm, "mid": v(-70.87, -55.15) * mm, "end": v(-70.66, -55.74) * mm});
            skArc(sketch, "E13.40.0", {"start": v(-68.95, -57.84) * mm, "mid": v(-68.42, -58.17) * mm, "end": v(-67.79, -58.11) * mm});
            skLineSegment(sketch, "E13.40.1", {"start": v(-65.6, -57.16) * mm, "end": v(-67.79, -58.11) * mm});
            skLineSegment(sketch, "E13.40.2", {"start": v(-64.17, -55.82) * mm, "end": v(-67.03, -58.5) * mm});
            skArc(sketch, "E13.40.3", {"start": v(-60.07, -60.2) * mm, "mid": v(-59.93, -55.97) * mm, "end": v(-64.17, -55.82) * mm});
            skLineSegment(sketch, "E13.40.4", {"start": v(-60.07, -60.2) * mm, "end": v(-62.93, -62.88) * mm});
            skLineSegment(sketch, "E13.40.5", {"start": v(-61.5, -61.54) * mm, "end": v(-62.6, -63.66) * mm});
            skArc(sketch, "E13.40.6", {"start": v(-62.6, -63.66) * mm, "mid": v(-62.7, -64.29) * mm, "end": v(-62.41, -64.85) * mm});
            skArc(sketch, "E13.41.0", {"start": v(-60.44, -66.7) * mm, "mid": v(-59.86, -66.94) * mm, "end": v(-59.24, -66.8) * mm});
            skLineSegment(sketch, "E13.41.1", {"start": v(-57.2, -65.56) * mm, "end": v(-59.24, -66.8) * mm});
            skLineSegment(sketch, "E13.41.2", {"start": v(-55.97, -64.04) * mm, "end": v(-58.44, -67.08) * mm});
            skArc(sketch, "E13.41.3", {"start": v(-51.32, -67.83) * mm, "mid": v(-51.75, -63.6) * mm, "end": v(-55.97, -64.04) * mm});
            skLineSegment(sketch, "E13.41.4", {"start": v(-51.32, -67.83) * mm, "end": v(-53.78, -70.86) * mm});
            skLineSegment(sketch, "E13.41.5", {"start": v(-52.55, -69.35) * mm, "end": v(-53.35, -71.6) * mm});
            skArc(sketch, "E13.41.6", {"start": v(-53.35, -71.6) * mm, "mid": v(-53.37, -72.23) * mm, "end": v(-53, -72.74) * mm});
            skArc(sketch, "E13.42.0", {"start": v(-50.8, -74.3) * mm, "mid": v(-50.18, -74.47) * mm, "end": v(-49.6, -74.25) * mm});
            skLineSegment(sketch, "E13.42.1", {"start": v(-47.74, -72.74) * mm, "end": v(-49.6, -74.25) * mm});
            skLineSegment(sketch, "E13.42.2", {"start": v(-46.73, -71.07) * mm, "end": v(-48.76, -74.4) * mm});
            skArc(sketch, "E13.42.3", {"start": v(-41.6, -74.18) * mm, "mid": v(-42.6, -70.06) * mm, "end": v(-46.73, -71.07) * mm});
            skLineSegment(sketch, "E13.42.4", {"start": v(-41.6, -74.18) * mm, "end": v(-43.63, -77.53) * mm});
            skLineSegment(sketch, "E13.42.5", {"start": v(-42.62, -75.85) * mm, "end": v(-43.1, -78.2) * mm});
            skArc(sketch, "E13.42.6", {"start": v(-43.1, -78.2) * mm, "mid": v(-43.03, -78.82) * mm, "end": v(-42.6, -79.28) * mm});
            skArc(sketch, "E13.43.0", {"start": v(-40.2, -80.52) * mm, "mid": v(-39.58, -80.61) * mm, "end": v(-39.02, -80.3) * mm});
            skLineSegment(sketch, "E13.43.1", {"start": v(-37.4, -78.56) * mm, "end": v(-39.02, -80.3) * mm});
            skLineSegment(sketch, "E13.43.2", {"start": v(-36.62, -76.77) * mm, "end": v(-38.17, -80.35) * mm});
            skArc(sketch, "E13.43.3", {"start": v(-31.11, -79.16) * mm, "mid": v(-32.67, -75.21) * mm, "end": v(-36.62, -76.77) * mm});
            skLineSegment(sketch, "E13.43.4", {"start": v(-31.11, -79.16) * mm, "end": v(-32.67, -82.74) * mm});
            skLineSegment(sketch, "E13.43.5", {"start": v(-31.9, -80.95) * mm, "end": v(-32.06, -83.33) * mm});
            skArc(sketch, "E13.43.6", {"start": v(-32.06, -83.33) * mm, "mid": v(-31.9, -83.95) * mm, "end": v(-31.4, -84.34) * mm});
            skArc(sketch, "E13.44.0", {"start": v(-28.86, -85.25) * mm, "mid": v(-28.23, -85.25) * mm, "end": v(-27.72, -84.87) * mm});
            skLineSegment(sketch, "E13.44.1", {"start": v(-26.35, -82.92) * mm, "end": v(-27.72, -84.87) * mm});
            skLineSegment(sketch, "E13.44.2", {"start": v(-25.82, -81.04) * mm, "end": v(-26.88, -84.8) * mm});
            skArc(sketch, "E13.44.3", {"start": v(-20.04, -82.66) * mm, "mid": v(-22.12, -78.96) * mm, "end": v(-25.82, -81.04) * mm});
            skLineSegment(sketch, "E13.44.4", {"start": v(-20.04, -82.66) * mm, "end": v(-21.1, -86.42) * mm});
            skLineSegment(sketch, "E13.44.5", {"start": v(-20.57, -84.54) * mm, "end": v(-20.41, -86.92) * mm});
            skArc(sketch, "E13.44.6", {"start": v(-20.41, -86.92) * mm, "mid": v(-20.17, -87.5) * mm, "end": v(-19.63, -87.83) * mm});
            skArc(sketch, "E13.45.0", {"start": v(-16.99, -88.38) * mm, "mid": v(-16.36, -88.3) * mm, "end": v(-15.9, -87.86) * mm});
            skLineSegment(sketch, "E13.45.1", {"start": v(-14.81, -85.74) * mm, "end": v(-15.9, -87.86) * mm});
            skLineSegment(sketch, "E13.45.2", {"start": v(-14.55, -83.8) * mm, "end": v(-15.08, -87.67) * mm});
            skArc(sketch, "E13.45.3", {"start": v(-8.6, -84.62) * mm, "mid": v(-11.17, -81.24) * mm, "end": v(-14.55, -83.8) * mm});
            skLineSegment(sketch, "E13.45.4", {"start": v(-8.6, -84.62) * mm, "end": v(-9.13, -88.5) * mm});
            skLineSegment(sketch, "E13.45.5", {"start": v(-8.87, -86.55) * mm, "end": v(-8.39, -88.9) * mm});
            skArc(sketch, "E13.45.6", {"start": v(-8.39, -88.9) * mm, "mid": v(-8.07, -89.44) * mm, "end": v(-7.49, -89.69) * mm});
            skLineSegment(sketch, "E14", {"start": v(3, -86.96) * mm, "end": v(3, -85) * mm});
            skArc(sketch, "E15", {"start": v(-8.6, -84.62) * mm, "mid": v(-6, -87.8) * mm, "end": v(-3, -85) * mm});
            skArc(sketch, "E16.1.0", {"start": v(3, -85) * mm, "mid": v(6, -87.8) * mm, "end": v(8.6, -84.62) * mm});
            skArc(sketch, "E16.2.0", {"start": v(14.55, -83.8) * mm, "mid": v(17.9, -86.17) * mm, "end": v(20.04, -82.66) * mm});
            skArc(sketch, "E16.3.0", {"start": v(25.82, -81.04) * mm, "mid": v(29.47, -82.93) * mm, "end": v(31.11, -79.16) * mm});
            skArc(sketch, "E16.4.0", {"start": v(36.62, -76.77) * mm, "mid": v(40.5, -78.15) * mm, "end": v(41.6, -74.18) * mm});
            skArc(sketch, "E16.5.0", {"start": v(46.73, -71.07) * mm, "mid": v(50.76, -71.9) * mm, "end": v(51.32, -67.83) * mm});
            skArc(sketch, "E16.6.0", {"start": v(55.97, -64.04) * mm, "mid": v(60.07, -64.32) * mm, "end": v(60.07, -60.2) * mm});
            skArc(sketch, "E16.7.0", {"start": v(64.17, -55.82) * mm, "mid": v(68.27, -55.54) * mm, "end": v(67.71, -51.47) * mm});
            skArc(sketch, "E16.8.0", {"start": v(71.17, -46.57) * mm, "mid": v(75.2, -45.73) * mm, "end": v(74.1, -41.77) * mm});
            skArc(sketch, "E16.9.0", {"start": v(76.85, -36.44) * mm, "mid": v(80.73, -35.06) * mm, "end": v(79.09, -31.3) * mm});
            skArc(sketch, "E16.10.0", {"start": v(81.1, -25.64) * mm, "mid": v(84.75, -23.75) * mm, "end": v(82.61, -20.23) * mm});
            skArc(sketch, "E16.11.0", {"start": v(83.83, -14.36) * mm, "mid": v(87.2, -11.98) * mm, "end": v(84.6, -8.8) * mm});
            skArc(sketch, "E16.12.0", {"start": v(85, -2.8) * mm, "mid": v(88.01, 0) * mm, "end": v(85, 2.8) * mm});
            skArc(sketch, "E16.13.0", {"start": v(84.6, 8.8) * mm, "mid": v(87.2, 11.98) * mm, "end": v(83.83, 14.36) * mm});
            skArc(sketch, "E16.14.0", {"start": v(82.61, 20.23) * mm, "mid": v(84.75, 23.75) * mm, "end": v(81.1, 25.64) * mm});
            skArc(sketch, "E16.15.0", {"start": v(79.09, 31.3) * mm, "mid": v(80.73, 35.06) * mm, "end": v(76.85, 36.44) * mm});
            skArc(sketch, "E16.16.0", {"start": v(74.1, 41.77) * mm, "mid": v(75.2, 45.73) * mm, "end": v(71.17, 46.57) * mm});
            skArc(sketch, "E16.17.0", {"start": v(67.71, 51.47) * mm, "mid": v(68.27, 55.54) * mm, "end": v(64.17, 55.82) * mm});
            skArc(sketch, "E16.18.0", {"start": v(60.07, 60.2) * mm, "mid": v(60.07, 64.32) * mm, "end": v(55.97, 64.04) * mm});
            skArc(sketch, "E16.19.0", {"start": v(51.32, 67.83) * mm, "mid": v(50.76, 71.9) * mm, "end": v(46.73, 71.07) * mm});
            skArc(sketch, "E16.20.0", {"start": v(41.6, 74.18) * mm, "mid": v(40.5, 78.15) * mm, "end": v(36.62, 76.77) * mm});
            skArc(sketch, "E16.21.0", {"start": v(31.11, 79.16) * mm, "mid": v(29.47, 82.93) * mm, "end": v(25.82, 81.04) * mm});
            skArc(sketch, "E16.22.0", {"start": v(20.04, 82.66) * mm, "mid": v(17.9, 86.17) * mm, "end": v(14.55, 83.8) * mm});
            skArc(sketch, "E16.23.0", {"start": v(8.6, 84.62) * mm, "mid": v(6, 87.8) * mm, "end": v(3, 85) * mm});
            skArc(sketch, "E16.24.0", {"start": v(-3, 85) * mm, "mid": v(-6, 87.8) * mm, "end": v(-8.6, 84.62) * mm});
            skArc(sketch, "E16.25.0", {"start": v(-14.55, 83.8) * mm, "mid": v(-17.9, 86.17) * mm, "end": v(-20.04, 82.66) * mm});
            skArc(sketch, "E16.26.0", {"start": v(-25.82, 81.04) * mm, "mid": v(-29.47, 82.93) * mm, "end": v(-31.11, 79.16) * mm});
            skArc(sketch, "E16.27.0", {"start": v(-36.62, 76.77) * mm, "mid": v(-40.5, 78.15) * mm, "end": v(-41.6, 74.18) * mm});
            skArc(sketch, "E16.28.0", {"start": v(-46.73, 71.07) * mm, "mid": v(-50.76, 71.9) * mm, "end": v(-51.32, 67.83) * mm});
            skArc(sketch, "E16.29.0", {"start": v(-55.97, 64.04) * mm, "mid": v(-60.07, 64.32) * mm, "end": v(-60.07, 60.2) * mm});
            skArc(sketch, "E16.30.0", {"start": v(-64.17, 55.82) * mm, "mid": v(-68.27, 55.54) * mm, "end": v(-67.71, 51.47) * mm});
            skArc(sketch, "E16.31.0", {"start": v(-71.17, 46.57) * mm, "mid": v(-75.2, 45.73) * mm, "end": v(-74.1, 41.77) * mm});
            skArc(sketch, "E16.32.0", {"start": v(-76.85, 36.44) * mm, "mid": v(-80.73, 35.06) * mm, "end": v(-79.09, 31.3) * mm});
            skArc(sketch, "E16.33.0", {"start": v(-81.1, 25.64) * mm, "mid": v(-84.75, 23.75) * mm, "end": v(-82.61, 20.23) * mm});
            skArc(sketch, "E16.34.0", {"start": v(-83.83, 14.36) * mm, "mid": v(-87.2, 11.98) * mm, "end": v(-84.6, 8.8) * mm});
            skArc(sketch, "E16.35.0", {"start": v(-85, 2.8) * mm, "mid": v(-88.01, 0) * mm, "end": v(-85, -2.8) * mm});
            skArc(sketch, "E16.36.0", {"start": v(-84.6, -8.8) * mm, "mid": v(-87.2, -11.98) * mm, "end": v(-83.83, -14.36) * mm});
            skArc(sketch, "E16.37.0", {"start": v(-82.61, -20.23) * mm, "mid": v(-84.75, -23.75) * mm, "end": v(-81.1, -25.64) * mm});
            skArc(sketch, "E16.38.0", {"start": v(-79.09, -31.3) * mm, "mid": v(-80.73, -35.06) * mm, "end": v(-76.85, -36.44) * mm});
            skArc(sketch, "E16.39.0", {"start": v(-74.1, -41.77) * mm, "mid": v(-75.2, -45.73) * mm, "end": v(-71.17, -46.57) * mm});
            skArc(sketch, "E16.40.0", {"start": v(-67.71, -51.47) * mm, "mid": v(-68.27, -55.54) * mm, "end": v(-64.17, -55.82) * mm});
            skArc(sketch, "E16.41.0", {"start": v(-60.07, -60.2) * mm, "mid": v(-60.07, -64.32) * mm, "end": v(-55.97, -64.04) * mm});
            skArc(sketch, "E16.42.0", {"start": v(-51.32, -67.83) * mm, "mid": v(-50.76, -71.9) * mm, "end": v(-46.73, -71.07) * mm});
            skArc(sketch, "E16.43.0", {"start": v(-41.6, -74.18) * mm, "mid": v(-40.5, -78.15) * mm, "end": v(-36.62, -76.77) * mm});
            skArc(sketch, "E16.44.0", {"start": v(-31.11, -79.16) * mm, "mid": v(-29.47, -82.93) * mm, "end": v(-25.82, -81.04) * mm});
            skArc(sketch, "E16.45.0", {"start": v(-20.04, -82.66) * mm, "mid": v(-17.9, -86.17) * mm, "end": v(-14.55, -83.8) * mm});
            skSolve(sketch);
        }
        {
            var Q0;
            Q0=makeQuery(id+"F0.imprint","IMPRINT",FACE,{"disambiguationData":[TD([[makeQuery(id+"F0.imprint","IMPRINT",EDGE,{"derivedFrom":sQuery(id+"F0.wireOp",EDGE,"E1")}),-1.0]])]});
            var Q1;
            Q1=makeQuery(id+"F0.imprint","IMPRINT",FACE,{"disambiguationData":[TD([[makeQuery(id+"F0.imprint","IMPRINT",EDGE,{"derivedFrom":sQuery(id+"F0.wireOp",EDGE,"E0")}),-1.0]])]});
            extrude(context, id + "F1", {"entities" : qUnion([Q0, Q1]), "depth" : 9 * mm, "offsetDistance" : 25 * mm});
        }
        {
            var Q0;
            Q0=makeQuery(id+"F1.opExtrude","CAP_FACE",FACE,{"disambiguationData":[OSD([sQuery(id+"F0.wireOp",EDGE,"E0"),sQuery(id+"F0.wireOp",EDGE,"E3"),sQuery(id+"F0.wireOp",EDGE,"E13.1.3"),sQuery(id+"F0.wireOp",EDGE,"E13.2.3"),sQuery(id+"F0.wireOp",EDGE,"E13.3.3"),sQuery(id+"F0.wireOp",EDGE,"E13.4.3"),sQuery(id+"F0.wireOp",EDGE,"E13.5.3"),sQuery(id+"F0.wireOp",EDGE,"E13.6.3"),sQuery(id+"F0.wireOp",EDGE,"E13.7.3"),sQuery(id+"F0.wireOp",EDGE,"E13.8.3"),sQuery(id+"F0.wireOp",EDGE,"E13.9.3"),sQuery(id+"F0.wireOp",EDGE,"E13.10.3"),sQuery(id+"F0.wireOp",EDGE,"E13.11.3"),sQuery(id+"F0.wireOp",EDGE,"E13.12.3"),sQuery(id+"F0.wireOp",EDGE,"E13.13.3"),sQuery(id+"F0.wireOp",EDGE,"E13.14.3"),sQuery(id+"F0.wireOp",EDGE,"E13.15.3"),sQuery(id+"F0.wireOp",EDGE,"E13.16.3"),sQuery(id+"F0.wireOp",EDGE,"E13.17.3"),sQuery(id+"F0.wireOp",EDGE,"E13.18.3"),sQuery(id+"F0.wireOp",EDGE,"E13.19.3"),sQuery(id+"F0.wireOp",EDGE,"E13.20.3"),sQuery(id+"F0.wireOp",EDGE,"E13.21.3"),sQuery(id+"F0.wireOp",EDGE,"E13.22.3"),sQuery(id+"F0.wireOp",EDGE,"E8.1.2"),sQuery(id+"F0.wireOp",EDGE,"E13.24.3"),sQuery(id+"F0.wireOp",EDGE,"E13.25.3"),sQuery(id+"F0.wireOp",EDGE,"E13.26.3"),sQuery(id+"F0.wireOp",EDGE,"E13.27.3"),sQuery(id+"F0.wireOp",EDGE,"E13.28.3"),sQuery(id+"F0.wireOp",EDGE,"E13.29.3"),sQuery(id+"F0.wireOp",EDGE,"E13.30.3"),sQuery(id+"F0.wireOp",EDGE,"E13.31.3"),sQuery(id+"F0.wireOp",EDGE,"E13.32.3"),sQuery(id+"F0.wireOp",EDGE,"E13.33.3"),sQuery(id+"F0.wireOp",EDGE,"E13.34.3"),sQuery(id+"F0.wireOp",EDGE,"E13.35.3"),sQuery(id+"F0.wireOp",EDGE,"E13.36.3"),sQuery(id+"F0.wireOp",EDGE,"E13.37.3"),sQuery(id+"F0.wireOp",EDGE,"E13.38.3"),sQuery(id+"F0.wireOp",EDGE,"E13.39.3"),sQuery(id+"F0.wireOp",EDGE,"E13.40.3"),sQuery(id+"F0.wireOp",EDGE,"E13.41.3"),sQuery(id+"F0.wireOp",EDGE,"E13.42.3"),sQuery(id+"F0.wireOp",EDGE,"E13.43.3"),sQuery(id+"F0.wireOp",EDGE,"E13.44.3"),sQuery(id+"F0.wireOp",EDGE,"E13.45.3"),sQuery(id+"F0.wireOp",EDGE,"E15"),sQuery(id+"F0.wireOp",EDGE,"E16.1.0"),sQuery(id+"F0.wireOp",EDGE,"E16.2.0"),sQuery(id+"F0.wireOp",EDGE,"E16.3.0"),sQuery(id+"F0.wireOp",EDGE,"E16.4.0"),sQuery(id+"F0.wireOp",EDGE,"E16.5.0"),sQuery(id+"F0.wireOp",EDGE,"E16.6.0"),sQuery(id+"F0.wireOp",EDGE,"E16.7.0"),sQuery(id+"F0.wireOp",EDGE,"E16.8.0"),sQuery(id+"F0.wireOp",EDGE,"E16.9.0"),sQuery(id+"F0.wireOp",EDGE,"E16.10.0"),sQuery(id+"F0.wireOp",EDGE,"E16.11.0"),sQuery(id+"F0.wireOp",EDGE,"E16.12.0"),sQuery(id+"F0.wireOp",EDGE,"E16.13.0"),sQuery(id+"F0.wireOp",EDGE,"E16.14.0"),sQuery(id+"F0.wireOp",EDGE,"E16.15.0"),sQuery(id+"F0.wireOp",EDGE,"E16.16.0"),sQuery(id+"F0.wireOp",EDGE,"E16.17.0"),sQuery(id+"F0.wireOp",EDGE,"E16.18.0"),sQuery(id+"F0.wireOp",EDGE,"E16.19.0"),sQuery(id+"F0.wireOp",EDGE,"E16.20.0"),sQuery(id+"F0.wireOp",EDGE,"E16.21.0"),sQuery(id+"F0.wireOp",EDGE,"E16.22.0"),sQuery(id+"F0.wireOp",EDGE,"E16.23.0"),sQuery(id+"F0.wireOp",EDGE,"E16.24.0"),sQuery(id+"F0.wireOp",EDGE,"E16.25.0"),sQuery(id+"F0.wireOp",EDGE,"E16.26.0"),sQuery(id+"F0.wireOp",EDGE,"E16.27.0"),sQuery(id+"F0.wireOp",EDGE,"E16.28.0"),sQuery(id+"F0.wireOp",EDGE,"E16.29.0"),sQuery(id+"F0.wireOp",EDGE,"E16.30.0"),sQuery(id+"F0.wireOp",EDGE,"E16.31.0"),sQuery(id+"F0.wireOp",EDGE,"E16.32.0"),sQuery(id+"F0.wireOp",EDGE,"E16.33.0"),sQuery(id+"F0.wireOp",EDGE,"E16.34.0"),sQuery(id+"F0.wireOp",EDGE,"E16.35.0"),sQuery(id+"F0.wireOp",EDGE,"E16.36.0"),sQuery(id+"F0.wireOp",EDGE,"E16.37.0"),sQuery(id+"F0.wireOp",EDGE,"E16.38.0"),sQuery(id+"F0.wireOp",EDGE,"E16.39.0"),sQuery(id+"F0.wireOp",EDGE,"E16.40.0"),sQuery(id+"F0.wireOp",EDGE,"E16.41.0"),sQuery(id+"F0.wireOp",EDGE,"E16.42.0"),sQuery(id+"F0.wireOp",EDGE,"E16.43.0"),sQuery(id+"F0.wireOp",EDGE,"E16.44.0"),sQuery(id+"F0.wireOp",EDGE,"E16.45.0")])],"isStart":false});
            var sketch = newSketch(context, id + "F2", { "sketchPlane" : qUnion([Q0])});
            skArc(sketch, "E17.0", {"start": v(-55.97, 64.04) * mm, "mid": v(-51.75, 63.6) * mm, "end": v(-51.32, 67.83) * mm});
            skArc(sketch, "E18.0", {"start": v(-46.73, 71.07) * mm, "mid": v(-50.76, 71.9) * mm, "end": v(-51.32, 67.83) * mm});
            skArc(sketch, "E19.0", {"start": v(-46.73, 71.07) * mm, "mid": v(-42.6, 70.06) * mm, "end": v(-41.6, 74.18) * mm});
            skArc(sketch, "E20.0", {"start": v(-55.97, 64.04) * mm, "mid": v(-60.07, 64.32) * mm, "end": v(-60.07, 60.2) * mm});
            skArc(sketch, "E21.0", {"start": v(-64.17, 55.82) * mm, "mid": v(-59.93, 55.97) * mm, "end": v(-60.07, 60.2) * mm});
            skArc(sketch, "E22.0", {"start": v(-64.17, 55.82) * mm, "mid": v(-68.27, 55.54) * mm, "end": v(-67.71, 51.47) * mm});
            skArc(sketch, "E23.0", {"start": v(-71.17, 46.57) * mm, "mid": v(-67, 47.29) * mm, "end": v(-67.71, 51.47) * mm});
            skArc(sketch, "E24.0", {"start": v(-71.17, 46.57) * mm, "mid": v(-75.2, 45.73) * mm, "end": v(-74.1, 41.77) * mm});
            skArc(sketch, "E25.0", {"start": v(-76.85, 36.44) * mm, "mid": v(-72.8, 37.73) * mm, "end": v(-74.1, 41.77) * mm});
            skArc(sketch, "E26.0", {"start": v(-76.85, 36.44) * mm, "mid": v(-80.73, 35.06) * mm, "end": v(-79.09, 31.3) * mm});
            skArc(sketch, "E27.0", {"start": v(-81.1, 25.64) * mm, "mid": v(-77.27, 27.46) * mm, "end": v(-79.09, 31.3) * mm});
            skArc(sketch, "E28.0", {"start": v(-81.1, 25.64) * mm, "mid": v(-84.75, 23.75) * mm, "end": v(-82.61, 20.23) * mm});
            skArc(sketch, "E29.0", {"start": v(-83.83, 14.36) * mm, "mid": v(-80.28, 16.68) * mm, "end": v(-82.61, 20.23) * mm});
            skArc(sketch, "E30.0", {"start": v(-83.83, 14.36) * mm, "mid": v(-87.2, 11.98) * mm, "end": v(-84.6, 8.8) * mm});
            skArc(sketch, "E31.0", {"start": v(-85, 2.8) * mm, "mid": v(-81.8, 5.6) * mm, "end": v(-84.6, 8.8) * mm});
            skArc(sketch, "E32.0", {"start": v(-85, 2.8) * mm, "mid": v(-88.01, 0) * mm, "end": v(-85, -2.8) * mm});
            skArc(sketch, "E33.0", {"start": v(-84.6, -8.8) * mm, "mid": v(-81.8, -5.6) * mm, "end": v(-85, -2.8) * mm});
            skArc(sketch, "E34.0", {"start": v(-84.6, -8.8) * mm, "mid": v(-87.2, -11.98) * mm, "end": v(-83.83, -14.36) * mm});
            skArc(sketch, "E35.0", {"start": v(-82.61, -20.23) * mm, "mid": v(-80.28, -16.68) * mm, "end": v(-83.83, -14.36) * mm});
            skArc(sketch, "E36.0", {"start": v(-82.61, -20.23) * mm, "mid": v(-84.75, -23.75) * mm, "end": v(-81.1, -25.64) * mm});
            skArc(sketch, "E37.0", {"start": v(-79.09, -31.3) * mm, "mid": v(-77.27, -27.46) * mm, "end": v(-81.1, -25.64) * mm});
            skArc(sketch, "E38.0", {"start": v(-79.09, -31.3) * mm, "mid": v(-80.73, -35.06) * mm, "end": v(-76.85, -36.44) * mm});
            skArc(sketch, "E39.0", {"start": v(-74.1, -41.77) * mm, "mid": v(-72.8, -37.73) * mm, "end": v(-76.85, -36.44) * mm});
            skArc(sketch, "E40.0", {"start": v(-74.1, -41.77) * mm, "mid": v(-75.2, -45.73) * mm, "end": v(-71.17, -46.57) * mm});
            skArc(sketch, "E41.0", {"start": v(-67.71, -51.47) * mm, "mid": v(-67, -47.29) * mm, "end": v(-71.17, -46.57) * mm});
            skArc(sketch, "E42.0", {"start": v(-67.71, -51.47) * mm, "mid": v(-68.27, -55.54) * mm, "end": v(-64.17, -55.82) * mm});
            skArc(sketch, "E43.0", {"start": v(-60.07, -60.2) * mm, "mid": v(-59.93, -55.97) * mm, "end": v(-64.17, -55.82) * mm});
            skArc(sketch, "E44.0", {"start": v(-60.07, -60.2) * mm, "mid": v(-60.07, -64.32) * mm, "end": v(-55.97, -64.04) * mm});
            skArc(sketch, "E45.0", {"start": v(-51.32, -67.83) * mm, "mid": v(-51.75, -63.6) * mm, "end": v(-55.97, -64.04) * mm});
            skPoint(sketch, "E46.0", {"position": v(-50.76, -71.9) * mm});
            skArc(sketch, "E47.0", {"start": v(-51.32, -67.83) * mm, "mid": v(-50.76, -71.9) * mm, "end": v(-46.73, -71.07) * mm});
            skArc(sketch, "E48.0", {"start": v(-41.6, -74.18) * mm, "mid": v(-42.6, -70.06) * mm, "end": v(-46.73, -71.07) * mm});
            skArc(sketch, "E49.0", {"start": v(-41.6, -74.18) * mm, "mid": v(-40.5, -78.15) * mm, "end": v(-36.62, -76.77) * mm});
            skArc(sketch, "E50.0", {"start": v(-31.11, -79.16) * mm, "mid": v(-32.67, -75.21) * mm, "end": v(-36.62, -76.77) * mm});
            skArc(sketch, "E51.0", {"start": v(-31.11, -79.16) * mm, "mid": v(-29.47, -82.93) * mm, "end": v(-25.82, -81.04) * mm});
            skArc(sketch, "E52.0", {"start": v(-20.04, -82.66) * mm, "mid": v(-22.12, -78.96) * mm, "end": v(-25.82, -81.04) * mm});
            skArc(sketch, "E53.0", {"start": v(-20.04, -82.66) * mm, "mid": v(-17.9, -86.17) * mm, "end": v(-14.55, -83.8) * mm});
            skArc(sketch, "E54.0", {"start": v(-8.6, -84.62) * mm, "mid": v(-11.17, -81.24) * mm, "end": v(-14.55, -83.8) * mm});
            skArc(sketch, "E55.0", {"start": v(-8.6, -84.62) * mm, "mid": v(-6, -87.8) * mm, "end": v(-3, -85) * mm});
            skArc(sketch, "E56.0", {"start": v(3, -85) * mm, "mid": v(0, -82) * mm, "end": v(-3, -85) * mm});
            skArc(sketch, "E57.0", {"start": v(3, -85) * mm, "mid": v(6, -87.8) * mm, "end": v(8.6, -84.62) * mm});
            skArc(sketch, "E58.0", {"start": v(14.55, -83.8) * mm, "mid": v(11.17, -81.24) * mm, "end": v(8.6, -84.62) * mm});
            skArc(sketch, "E59.0", {"start": v(14.55, -83.8) * mm, "mid": v(17.9, -86.17) * mm, "end": v(20.04, -82.66) * mm});
            skArc(sketch, "E60.0", {"start": v(25.82, -81.04) * mm, "mid": v(22.12, -78.96) * mm, "end": v(20.04, -82.66) * mm});
            skArc(sketch, "E61.0", {"start": v(25.82, -81.04) * mm, "mid": v(29.47, -82.93) * mm, "end": v(31.11, -79.16) * mm});
            skArc(sketch, "E62.0", {"start": v(36.62, -76.77) * mm, "mid": v(32.67, -75.21) * mm, "end": v(31.11, -79.16) * mm});
            skArc(sketch, "E63.0", {"start": v(36.62, -76.77) * mm, "mid": v(40.5, -78.15) * mm, "end": v(41.6, -74.18) * mm});
            skArc(sketch, "E64.0", {"start": v(46.73, -71.07) * mm, "mid": v(42.6, -70.06) * mm, "end": v(41.6, -74.18) * mm});
            skArc(sketch, "E65.0", {"start": v(46.73, -71.07) * mm, "mid": v(50.76, -71.9) * mm, "end": v(51.32, -67.83) * mm});
            skArc(sketch, "E66.0", {"start": v(55.97, -64.04) * mm, "mid": v(51.75, -63.6) * mm, "end": v(51.32, -67.83) * mm});
            skArc(sketch, "E67.0", {"start": v(55.97, -64.04) * mm, "mid": v(60.07, -64.32) * mm, "end": v(60.07, -60.2) * mm});
            skPoint(sketch, "E68.0", {"position": v(60.07, -60.2) * mm});
            skArc(sketch, "E69.0", {"start": v(64.17, -55.82) * mm, "mid": v(59.93, -55.97) * mm, "end": v(60.07, -60.2) * mm});
            skArc(sketch, "E70.0", {"start": v(64.17, -55.82) * mm, "mid": v(68.27, -55.54) * mm, "end": v(67.71, -51.47) * mm});
            skArc(sketch, "E71.0", {"start": v(71.17, -46.57) * mm, "mid": v(67, -47.29) * mm, "end": v(67.71, -51.47) * mm});
            skArc(sketch, "E72.0", {"start": v(71.17, -46.57) * mm, "mid": v(75.2, -45.73) * mm, "end": v(74.1, -41.77) * mm});
            skArc(sketch, "E73.0", {"start": v(76.85, -36.44) * mm, "mid": v(72.8, -37.73) * mm, "end": v(74.1, -41.77) * mm});
            skArc(sketch, "E74.0", {"start": v(76.85, -36.44) * mm, "mid": v(80.73, -35.06) * mm, "end": v(79.09, -31.3) * mm});
            skArc(sketch, "E75.0", {"start": v(81.1, -25.64) * mm, "mid": v(77.27, -27.46) * mm, "end": v(79.09, -31.3) * mm});
            skArc(sketch, "E76.0", {"start": v(81.1, -25.64) * mm, "mid": v(84.75, -23.75) * mm, "end": v(82.61, -20.23) * mm});
            skArc(sketch, "E77.0", {"start": v(83.83, -14.36) * mm, "mid": v(87.2, -11.98) * mm, "end": v(84.6, -8.8) * mm});
            skArc(sketch, "E78.0", {"start": v(85, -2.8) * mm, "mid": v(88.01, 0) * mm, "end": v(85, 2.8) * mm});
            skArc(sketch, "E79.0", {"start": v(84.6, 8.8) * mm, "mid": v(87.2, 11.98) * mm, "end": v(83.83, 14.36) * mm});
            skArc(sketch, "E80.0", {"start": v(84.6, 8.8) * mm, "mid": v(81.8, 5.6) * mm, "end": v(85, 2.8) * mm});
            skArc(sketch, "E81.0", {"start": v(85, -2.8) * mm, "mid": v(81.8, -5.6) * mm, "end": v(84.6, -8.8) * mm});
            skArc(sketch, "E82.0", {"start": v(83.83, -14.36) * mm, "mid": v(80.28, -16.68) * mm, "end": v(82.61, -20.23) * mm});
            skArc(sketch, "E83.0", {"start": v(82.61, 20.23) * mm, "mid": v(80.28, 16.68) * mm, "end": v(83.83, 14.36) * mm});
            skArc(sketch, "E84.0", {"start": v(79.09, 31.3) * mm, "mid": v(77.27, 27.46) * mm, "end": v(81.1, 25.64) * mm});
            skArc(sketch, "E85.0", {"start": v(74.1, 41.77) * mm, "mid": v(72.8, 37.73) * mm, "end": v(76.85, 36.44) * mm});
            skArc(sketch, "E86.0", {"start": v(67.71, 51.47) * mm, "mid": v(67, 47.29) * mm, "end": v(71.17, 46.57) * mm});
            skArc(sketch, "E87.0", {"start": v(60.07, 60.2) * mm, "mid": v(59.93, 55.97) * mm, "end": v(64.17, 55.82) * mm});
            skArc(sketch, "E88.0", {"start": v(51.32, 67.83) * mm, "mid": v(51.75, 63.6) * mm, "end": v(55.97, 64.04) * mm});
            skArc(sketch, "E89.0", {"start": v(60.07, 60.2) * mm, "mid": v(60.07, 64.32) * mm, "end": v(55.97, 64.04) * mm});
            skArc(sketch, "E90.0", {"start": v(67.71, 51.47) * mm, "mid": v(68.27, 55.54) * mm, "end": v(64.17, 55.82) * mm});
            skArc(sketch, "E91.0", {"start": v(74.1, 41.77) * mm, "mid": v(75.2, 45.73) * mm, "end": v(71.17, 46.57) * mm});
            skArc(sketch, "E92.0", {"start": v(79.09, 31.3) * mm, "mid": v(80.73, 35.06) * mm, "end": v(76.85, 36.44) * mm});
            skArc(sketch, "E93.0", {"start": v(82.61, 20.23) * mm, "mid": v(84.75, 23.75) * mm, "end": v(81.1, 25.64) * mm});
            skArc(sketch, "E94.0", {"start": v(-36.62, 76.77) * mm, "mid": v(-40.5, 78.15) * mm, "end": v(-41.6, 74.18) * mm});
            skArc(sketch, "E95.0", {"start": v(-36.62, 76.77) * mm, "mid": v(-32.67, 75.21) * mm, "end": v(-31.11, 79.16) * mm});
            skArc(sketch, "E96.0", {"start": v(-25.82, 81.04) * mm, "mid": v(-29.47, 82.93) * mm, "end": v(-31.11, 79.16) * mm});
            skArc(sketch, "E97.0", {"start": v(-25.82, 81.04) * mm, "mid": v(-22.12, 78.96) * mm, "end": v(-20.04, 82.66) * mm});
            skArc(sketch, "E98.0", {"start": v(-14.55, 83.8) * mm, "mid": v(-17.9, 86.17) * mm, "end": v(-20.04, 82.66) * mm});
            skArc(sketch, "E99.0", {"start": v(-14.55, 83.8) * mm, "mid": v(-11.17, 81.24) * mm, "end": v(-8.6, 84.62) * mm});
            skArc(sketch, "E100.0", {"start": v(-3, 85) * mm, "mid": v(-6, 87.8) * mm, "end": v(-8.6, 84.62) * mm});
            skArc(sketch, "E101.0", {"start": v(-3, 85) * mm, "mid": v(0, 82) * mm, "end": v(3, 85) * mm});
            skArc(sketch, "E102.0", {"start": v(8.6, 84.62) * mm, "mid": v(6, 87.8) * mm, "end": v(3, 85) * mm});
            skArc(sketch, "E103.0", {"start": v(8.6, 84.62) * mm, "mid": v(11.17, 81.24) * mm, "end": v(14.55, 83.8) * mm});
            skArc(sketch, "E104.0", {"start": v(20.04, 82.66) * mm, "mid": v(17.9, 86.17) * mm, "end": v(14.55, 83.8) * mm});
            skArc(sketch, "E105.0", {"start": v(20.04, 82.66) * mm, "mid": v(22.12, 78.96) * mm, "end": v(25.82, 81.04) * mm});
            skArc(sketch, "E106.0", {"start": v(31.11, 79.16) * mm, "mid": v(29.47, 82.93) * mm, "end": v(25.82, 81.04) * mm});
            skArc(sketch, "E107.0", {"start": v(31.11, 79.16) * mm, "mid": v(32.67, 75.21) * mm, "end": v(36.62, 76.77) * mm});
            skArc(sketch, "E108.0", {"start": v(41.6, 74.18) * mm, "mid": v(40.5, 78.15) * mm, "end": v(36.62, 76.77) * mm});
            skArc(sketch, "E109.0", {"start": v(41.6, 74.18) * mm, "mid": v(42.6, 70.06) * mm, "end": v(46.73, 71.07) * mm});
            skArc(sketch, "E110.0", {"start": v(41.39, 74.31) * mm, "mid": v(40.38, 77.92) * mm, "end": v(36.85, 76.67) * mm});
            skArc(sketch, "E110.1", {"start": v(30.88, 79.26) * mm, "mid": v(32.57, 74.98) * mm, "end": v(36.85, 76.67) * mm});
            skArc(sketch, "E110.2", {"start": v(30.88, 79.26) * mm, "mid": v(29.39, 82.7) * mm, "end": v(26.06, 80.97) * mm});
            skArc(sketch, "E110.3", {"start": v(19.8, 82.72) * mm, "mid": v(22.06, 78.72) * mm, "end": v(26.06, 80.97) * mm});
            skArc(sketch, "E110.4", {"start": v(19.8, 82.72) * mm, "mid": v(17.86, 85.93) * mm, "end": v(14.8, 83.77) * mm});
            skArc(sketch, "E110.5", {"start": v(8.35, 84.65) * mm, "mid": v(11.13, 80.99) * mm, "end": v(14.8, 83.77) * mm});
            skArc(sketch, "E110.6", {"start": v(8.35, 84.65) * mm, "mid": v(5.99, 87.56) * mm, "end": v(3.25, 85) * mm});
            skArc(sketch, "E110.7", {"start": v(-3.25, 85) * mm, "mid": v(0, 81.75) * mm, "end": v(3.25, 85) * mm});
            skArc(sketch, "E110.8", {"start": v(-3.25, 85) * mm, "mid": v(-5.99, 87.56) * mm, "end": v(-8.35, 84.65) * mm});
            skArc(sketch, "E110.9", {"start": v(-14.8, 83.77) * mm, "mid": v(-11.13, 80.99) * mm, "end": v(-8.35, 84.65) * mm});
            skArc(sketch, "E110.10", {"start": v(-14.8, 83.77) * mm, "mid": v(-17.86, 85.93) * mm, "end": v(-19.8, 82.72) * mm});
            skArc(sketch, "E110.11", {"start": v(-26.06, 80.97) * mm, "mid": v(-22.06, 78.72) * mm, "end": v(-19.8, 82.72) * mm});
            skArc(sketch, "E110.12", {"start": v(-26.06, 80.97) * mm, "mid": v(-29.39, 82.7) * mm, "end": v(-30.88, 79.26) * mm});
            skArc(sketch, "E110.13", {"start": v(-36.85, 76.67) * mm, "mid": v(-32.57, 74.98) * mm, "end": v(-30.88, 79.26) * mm});
            skArc(sketch, "E110.14", {"start": v(-36.85, 76.67) * mm, "mid": v(-40.38, 77.92) * mm, "end": v(-41.39, 74.31) * mm});
            skArc(sketch, "E110.15", {"start": v(-46.94, 70.94) * mm, "mid": v(-42.48, 69.85) * mm, "end": v(-41.39, 74.31) * mm});
            skArc(sketch, "E110.16", {"start": v(-46.94, 70.94) * mm, "mid": v(-50.61, 71.7) * mm, "end": v(-51.12, 67.99) * mm});
            skArc(sketch, "E110.17", {"start": v(-56.16, 63.88) * mm, "mid": v(-51.6, 63.41) * mm, "end": v(-51.12, 67.99) * mm});
            skArc(sketch, "E110.18", {"start": v(-56.16, 63.88) * mm, "mid": v(-59.9, 64.14) * mm, "end": v(-59.9, 60.4) * mm});
            skArc(sketch, "E110.19", {"start": v(-64.34, 55.64) * mm, "mid": v(-59.75, 55.8) * mm, "end": v(-59.9, 60.4) * mm});
            skArc(sketch, "E110.20", {"start": v(-64.34, 55.64) * mm, "mid": v(-68.08, 55.39) * mm, "end": v(-67.57, 51.67) * mm});
            skArc(sketch, "E110.21", {"start": v(-71.32, 46.36) * mm, "mid": v(-66.79, 47.14) * mm, "end": v(-67.57, 51.67) * mm});
            skArc(sketch, "E110.22", {"start": v(-71.32, 46.36) * mm, "mid": v(-74.99, 45.6) * mm, "end": v(-73.98, 42) * mm});
            skArc(sketch, "E110.23", {"start": v(-76.97, 36.22) * mm, "mid": v(-72.58, 37.61) * mm, "end": v(-73.98, 42) * mm});
            skArc(sketch, "E110.24", {"start": v(-76.97, 36.22) * mm, "mid": v(-80.5, 34.96) * mm, "end": v(-79, 31.53) * mm});
            skArc(sketch, "E110.25", {"start": v(-81.18, 25.4) * mm, "mid": v(-77.03, 27.38) * mm, "end": v(-79, 31.53) * mm});
            skArc(sketch, "E110.26", {"start": v(-81.18, 25.4) * mm, "mid": v(-84.5, 23.68) * mm, "end": v(-82.56, 20.48) * mm});
            skArc(sketch, "E110.27", {"start": v(-83.88, 14.11) * mm, "mid": v(-80.04, 16.63) * mm, "end": v(-82.56, 20.48) * mm});
            skArc(sketch, "E110.28", {"start": v(-83.88, 14.11) * mm, "mid": v(-86.95, 11.95) * mm, "end": v(-84.58, 9.04) * mm});
            skArc(sketch, "E110.29", {"start": v(-85.02, 2.56) * mm, "mid": v(-81.56, 5.58) * mm, "end": v(-84.58, 9.04) * mm});
            skArc(sketch, "E110.30", {"start": v(-85.02, 2.56) * mm, "mid": v(-87.76, 0) * mm, "end": v(-85.02, -2.56) * mm});
            skArc(sketch, "E110.31", {"start": v(-84.58, -9.04) * mm, "mid": v(-81.56, -5.58) * mm, "end": v(-85.02, -2.56) * mm});
            skArc(sketch, "E110.32", {"start": v(-84.58, -9.04) * mm, "mid": v(-86.95, -11.95) * mm, "end": v(-83.88, -14.11) * mm});
            skArc(sketch, "E110.33", {"start": v(-82.56, -20.48) * mm, "mid": v(-80.04, -16.63) * mm, "end": v(-83.88, -14.11) * mm});
            skArc(sketch, "E110.34", {"start": v(-82.56, -20.48) * mm, "mid": v(-84.5, -23.68) * mm, "end": v(-81.18, -25.4) * mm});
            skArc(sketch, "E110.35", {"start": v(-79, -31.53) * mm, "mid": v(-77.03, -27.38) * mm, "end": v(-81.18, -25.4) * mm});
            skArc(sketch, "E110.36", {"start": v(-79, -31.53) * mm, "mid": v(-80.5, -34.96) * mm, "end": v(-76.97, -36.22) * mm});
            skArc(sketch, "E110.37", {"start": v(-73.98, -42) * mm, "mid": v(-72.58, -37.61) * mm, "end": v(-76.97, -36.22) * mm});
            skArc(sketch, "E110.38", {"start": v(-73.98, -42) * mm, "mid": v(-74.99, -45.6) * mm, "end": v(-71.32, -46.36) * mm});
            skArc(sketch, "E110.39", {"start": v(-67.57, -51.67) * mm, "mid": v(-66.79, -47.14) * mm, "end": v(-71.32, -46.36) * mm});
            skArc(sketch, "E110.40", {"start": v(-67.57, -51.67) * mm, "mid": v(-68.08, -55.39) * mm, "end": v(-64.34, -55.64) * mm});
            skArc(sketch, "E110.41", {"start": v(-59.9, -60.4) * mm, "mid": v(-59.75, -55.8) * mm, "end": v(-64.34, -55.64) * mm});
            skArc(sketch, "E110.42", {"start": v(-59.9, -60.4) * mm, "mid": v(-59.9, -64.14) * mm, "end": v(-56.16, -63.88) * mm});
            skArc(sketch, "E110.43", {"start": v(-51.12, -67.99) * mm, "mid": v(-51.6, -63.41) * mm, "end": v(-56.16, -63.88) * mm});
            skArc(sketch, "E110.44", {"start": v(-51.12, -67.99) * mm, "mid": v(-50.61, -71.7) * mm, "end": v(-46.94, -70.94) * mm});
            skArc(sketch, "E110.45", {"start": v(76.97, -36.22) * mm, "mid": v(72.58, -37.61) * mm, "end": v(73.98, -42) * mm});
            skArc(sketch, "E110.46", {"start": v(76.97, -36.22) * mm, "mid": v(80.5, -34.96) * mm, "end": v(79, -31.53) * mm});
            skArc(sketch, "E110.47", {"start": v(81.18, -25.4) * mm, "mid": v(77.03, -27.38) * mm, "end": v(79, -31.53) * mm});
            skArc(sketch, "E110.48", {"start": v(41.39, 74.31) * mm, "mid": v(42.48, 69.85) * mm, "end": v(46.94, 70.94) * mm});
            skArc(sketch, "E110.49", {"start": v(81.18, -25.4) * mm, "mid": v(84.5, -23.68) * mm, "end": v(82.56, -20.48) * mm});
            skArc(sketch, "E110.50", {"start": v(83.88, -14.11) * mm, "mid": v(80.04, -16.63) * mm, "end": v(82.56, -20.48) * mm});
            skArc(sketch, "E110.51", {"start": v(83.88, -14.11) * mm, "mid": v(86.95, -11.95) * mm, "end": v(84.58, -9.04) * mm});
            skArc(sketch, "E110.52", {"start": v(85.02, -2.56) * mm, "mid": v(81.56, -5.58) * mm, "end": v(84.58, -9.04) * mm});
            skArc(sketch, "E110.53", {"start": v(85.02, -2.56) * mm, "mid": v(87.76, 0) * mm, "end": v(85.02, 2.56) * mm});
            skArc(sketch, "E110.54", {"start": v(84.58, 9.04) * mm, "mid": v(81.56, 5.58) * mm, "end": v(85.02, 2.56) * mm});
            skArc(sketch, "E110.55", {"start": v(84.58, 9.04) * mm, "mid": v(86.95, 11.95) * mm, "end": v(83.88, 14.11) * mm});
            skArc(sketch, "E110.56", {"start": v(82.56, 20.48) * mm, "mid": v(80.04, 16.63) * mm, "end": v(83.88, 14.11) * mm});
            skArc(sketch, "E110.57", {"start": v(82.56, 20.48) * mm, "mid": v(84.5, 23.68) * mm, "end": v(81.18, 25.4) * mm});
            skArc(sketch, "E110.58", {"start": v(59.9, 60.4) * mm, "mid": v(59.75, 55.8) * mm, "end": v(64.34, 55.64) * mm});
            skArc(sketch, "E110.59", {"start": v(59.9, 60.4) * mm, "mid": v(59.9, 64.14) * mm, "end": v(56.16, 63.88) * mm});
            skArc(sketch, "E110.60", {"start": v(51.12, 67.99) * mm, "mid": v(51.6, 63.41) * mm, "end": v(56.16, 63.88) * mm});
            skArc(sketch, "E110.61", {"start": v(51.12, 67.99) * mm, "mid": v(50.61, 71.7) * mm, "end": v(46.94, 70.94) * mm});
            skArc(sketch, "E110.62", {"start": v(67.57, 51.67) * mm, "mid": v(68.08, 55.39) * mm, "end": v(64.34, 55.64) * mm});
            skArc(sketch, "E110.63", {"start": v(67.57, 51.67) * mm, "mid": v(66.79, 47.14) * mm, "end": v(71.32, 46.36) * mm});
            skArc(sketch, "E110.64", {"start": v(73.98, 42) * mm, "mid": v(74.99, 45.6) * mm, "end": v(71.32, 46.36) * mm});
            skArc(sketch, "E110.65", {"start": v(73.98, 42) * mm, "mid": v(72.58, 37.61) * mm, "end": v(76.97, 36.22) * mm});
            skArc(sketch, "E110.66", {"start": v(79, 31.53) * mm, "mid": v(80.5, 34.96) * mm, "end": v(76.97, 36.22) * mm});
            skArc(sketch, "E110.67", {"start": v(79, 31.53) * mm, "mid": v(77.03, 27.38) * mm, "end": v(81.18, 25.4) * mm});
            skArc(sketch, "E110.68", {"start": v(71.32, -46.36) * mm, "mid": v(74.99, -45.6) * mm, "end": v(73.98, -42) * mm});
            skArc(sketch, "E110.69", {"start": v(71.32, -46.36) * mm, "mid": v(66.79, -47.14) * mm, "end": v(67.57, -51.67) * mm});
            skArc(sketch, "E110.70", {"start": v(64.34, -55.64) * mm, "mid": v(68.08, -55.39) * mm, "end": v(67.57, -51.67) * mm});
            skArc(sketch, "E110.71", {"start": v(64.34, -55.64) * mm, "mid": v(59.75, -55.8) * mm, "end": v(59.9, -60.4) * mm});
            skArc(sketch, "E110.72", {"start": v(56.16, -63.88) * mm, "mid": v(59.9, -64.14) * mm, "end": v(59.9, -60.4) * mm});
            skArc(sketch, "E110.73", {"start": v(56.16, -63.88) * mm, "mid": v(51.6, -63.41) * mm, "end": v(51.12, -67.99) * mm});
            skArc(sketch, "E110.74", {"start": v(46.94, -70.94) * mm, "mid": v(50.61, -71.7) * mm, "end": v(51.12, -67.99) * mm});
            skArc(sketch, "E110.75", {"start": v(46.94, -70.94) * mm, "mid": v(42.48, -69.85) * mm, "end": v(41.39, -74.31) * mm});
            skArc(sketch, "E110.76", {"start": v(36.85, -76.67) * mm, "mid": v(40.38, -77.92) * mm, "end": v(41.39, -74.31) * mm});
            skArc(sketch, "E110.77", {"start": v(36.85, -76.67) * mm, "mid": v(32.57, -74.98) * mm, "end": v(30.88, -79.26) * mm});
            skArc(sketch, "E110.78", {"start": v(26.06, -80.97) * mm, "mid": v(29.39, -82.7) * mm, "end": v(30.88, -79.26) * mm});
            skArc(sketch, "E110.79", {"start": v(26.06, -80.97) * mm, "mid": v(22.06, -78.72) * mm, "end": v(19.8, -82.72) * mm});
            skArc(sketch, "E110.80", {"start": v(14.8, -83.77) * mm, "mid": v(17.86, -85.93) * mm, "end": v(19.8, -82.72) * mm});
            skArc(sketch, "E110.81", {"start": v(14.8, -83.77) * mm, "mid": v(11.13, -80.99) * mm, "end": v(8.35, -84.65) * mm});
            skArc(sketch, "E110.82", {"start": v(3.25, -85) * mm, "mid": v(5.99, -87.56) * mm, "end": v(8.35, -84.65) * mm});
            skArc(sketch, "E110.83", {"start": v(3.25, -85) * mm, "mid": v(0, -81.75) * mm, "end": v(-3.25, -85) * mm});
            skArc(sketch, "E110.84", {"start": v(-8.35, -84.65) * mm, "mid": v(-5.99, -87.56) * mm, "end": v(-3.25, -85) * mm});
            skArc(sketch, "E110.85", {"start": v(-8.35, -84.65) * mm, "mid": v(-11.13, -80.99) * mm, "end": v(-14.8, -83.77) * mm});
            skArc(sketch, "E110.86", {"start": v(-19.8, -82.72) * mm, "mid": v(-17.86, -85.93) * mm, "end": v(-14.8, -83.77) * mm});
            skArc(sketch, "E110.87", {"start": v(-19.8, -82.72) * mm, "mid": v(-22.06, -78.72) * mm, "end": v(-26.06, -80.97) * mm});
            skArc(sketch, "E110.88", {"start": v(-30.88, -79.26) * mm, "mid": v(-29.39, -82.7) * mm, "end": v(-26.06, -80.97) * mm});
            skArc(sketch, "E110.89", {"start": v(-30.88, -79.26) * mm, "mid": v(-32.57, -74.98) * mm, "end": v(-36.85, -76.67) * mm});
            skArc(sketch, "E110.90", {"start": v(-41.39, -74.31) * mm, "mid": v(-40.38, -77.92) * mm, "end": v(-36.85, -76.67) * mm});
            skArc(sketch, "E110.91", {"start": v(-41.39, -74.31) * mm, "mid": v(-42.48, -69.85) * mm, "end": v(-46.94, -70.94) * mm});
            skSolve(sketch);
        }
        {
            var Q0;
            Q0=makeQuery(id+"F2.imprint","IMPRINT",FACE,{"disambiguationData":[TD([[makeQuery(id+"F2.imprint","IMPRINT",EDGE,{"derivedFrom":sQuery(id+"F2.wireOp",EDGE,"E17.0")}),-1.0]])]});
            extrude(context, id + "F3", {"entities" : qUnion([Q0]), "operationType" : NewBodyOperationType.REMOVE, "oppositeDirection" : true, "depth" : 25 * mm, "offsetDistance" : 25 * mm});
        }
    });
